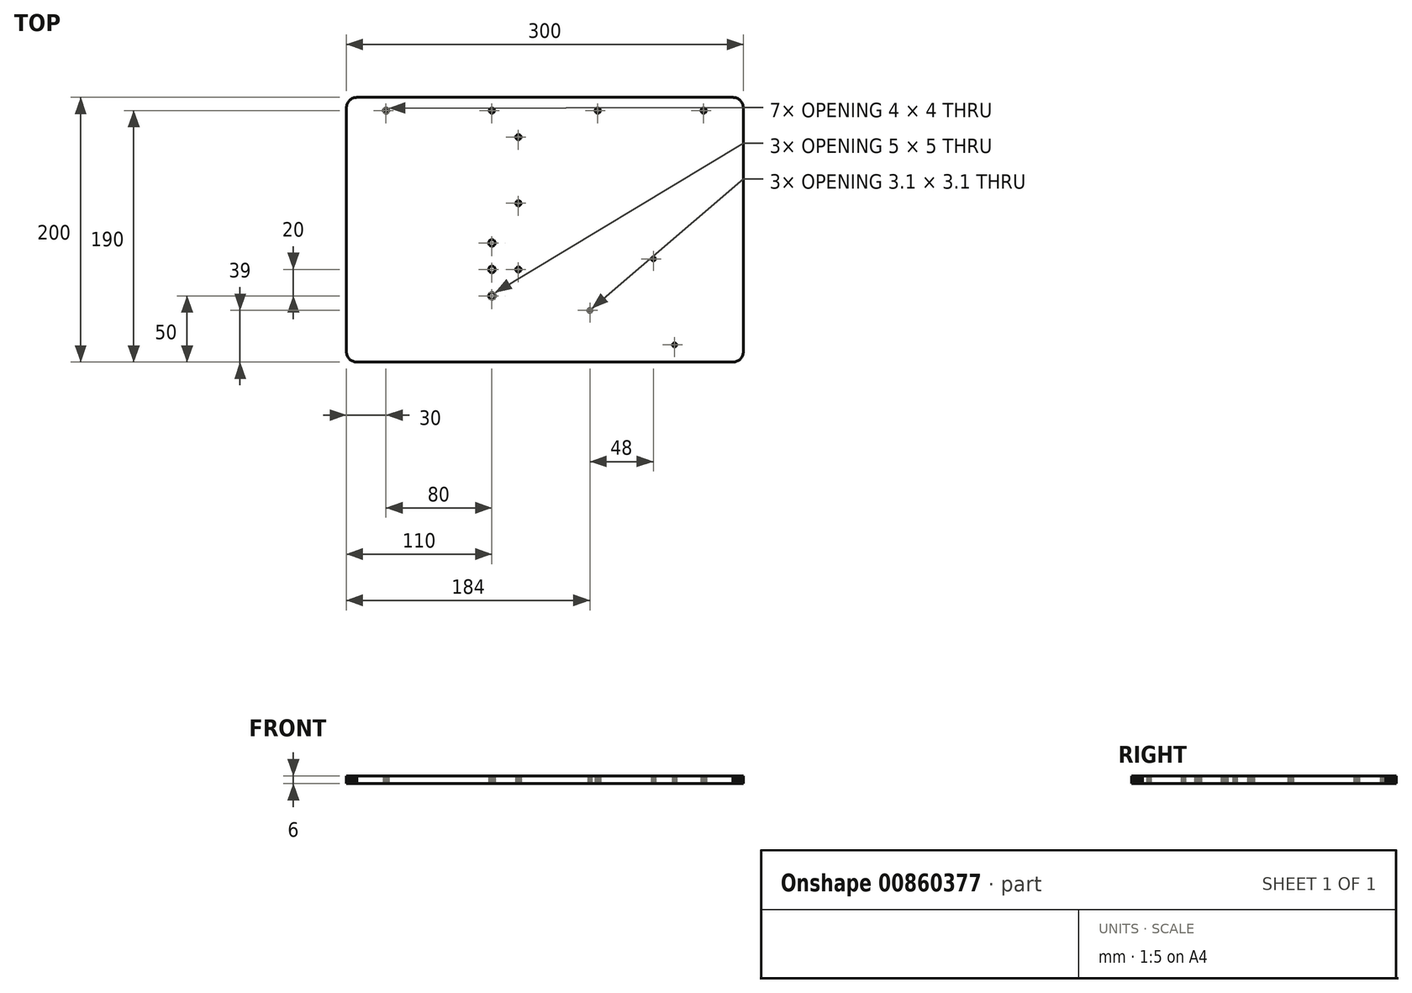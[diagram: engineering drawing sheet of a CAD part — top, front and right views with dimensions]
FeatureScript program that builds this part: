
annotation { "Feature Type Name" : "Feature", "Feature Type Description" : "" }
export const myFeature = defineFeature(function(context is Context, id is Id, definition is map)
    precondition{}
    {
        {
            var Q0;
            Q0=qCreatedBy(makeId("Top.planeOp"),FACE);
            var sketch = newSketch(context, id + "F0", { "sketchPlane" : qUnion([Q0])});
            skLineSegment(sketch, "E0", {"start": v(142.78, -99.96) * mm, "end": v(143.56, -99.85) * mm});
            skLineSegment(sketch, "E1", {"start": v(143.56, -99.85) * mm, "end": v(144.32, -99.66) * mm});
            skLineSegment(sketch, "E2", {"start": v(144.32, -99.66) * mm, "end": v(145.06, -99.4) * mm});
            skLineSegment(sketch, "E3", {"start": v(145.06, -99.4) * mm, "end": v(145.77, -99.06) * mm});
            skLineSegment(sketch, "E4", {"start": v(145.77, -99.06) * mm, "end": v(146.44, -98.65) * mm});
            skLineSegment(sketch, "E5", {"start": v(146.44, -98.65) * mm, "end": v(147.07, -98.18) * mm});
            skLineSegment(sketch, "E6", {"start": v(147.07, -98.18) * mm, "end": v(147.66, -97.66) * mm});
            skLineSegment(sketch, "E7", {"start": v(147.66, -97.66) * mm, "end": v(148.18, -97.08) * mm});
            skLineSegment(sketch, "E8", {"start": v(148.18, -97.08) * mm, "end": v(148.65, -96.44) * mm});
            skLineSegment(sketch, "E9", {"start": v(148.65, -96.44) * mm, "end": v(149.06, -95.77) * mm});
            skLineSegment(sketch, "E10", {"start": v(149.06, -95.77) * mm, "end": v(149.4, -95.06) * mm});
            skLineSegment(sketch, "E11", {"start": v(149.4, -95.06) * mm, "end": v(149.66, -94.32) * mm});
            skLineSegment(sketch, "E12", {"start": v(149.66, -94.32) * mm, "end": v(149.85, -93.56) * mm});
            skLineSegment(sketch, "E13", {"start": v(149.85, -93.56) * mm, "end": v(149.96, -92.78) * mm});
            skLineSegment(sketch, "E14", {"start": v(149.96, -92.78) * mm, "end": v(150, -92) * mm});
            skLineSegment(sketch, "E15", {"start": v(150, -92) * mm, "end": v(150, 92) * mm});
            skLineSegment(sketch, "E16", {"start": v(150, 92) * mm, "end": v(149.96, 92.78) * mm});
            skLineSegment(sketch, "E17", {"start": v(149.96, 92.78) * mm, "end": v(149.85, 93.56) * mm});
            skLineSegment(sketch, "E18", {"start": v(149.85, 93.56) * mm, "end": v(149.66, 94.32) * mm});
            skLineSegment(sketch, "E19", {"start": v(149.66, 94.32) * mm, "end": v(149.4, 95.06) * mm});
            skLineSegment(sketch, "E20", {"start": v(149.4, 95.06) * mm, "end": v(149.06, 95.77) * mm});
            skLineSegment(sketch, "E21", {"start": v(149.06, 95.77) * mm, "end": v(148.65, 96.44) * mm});
            skLineSegment(sketch, "E22", {"start": v(148.65, 96.44) * mm, "end": v(148.18, 97.07) * mm});
            skLineSegment(sketch, "E23", {"start": v(148.18, 97.07) * mm, "end": v(147.66, 97.66) * mm});
            skLineSegment(sketch, "E24", {"start": v(147.66, 97.66) * mm, "end": v(147.07, 98.18) * mm});
            skLineSegment(sketch, "E25", {"start": v(147.07, 98.18) * mm, "end": v(146.44, 98.65) * mm});
            skLineSegment(sketch, "E26", {"start": v(146.44, 98.65) * mm, "end": v(145.77, 99.06) * mm});
            skLineSegment(sketch, "E27", {"start": v(145.77, 99.06) * mm, "end": v(145.06, 99.4) * mm});
            skLineSegment(sketch, "E28", {"start": v(145.06, 99.4) * mm, "end": v(144.32, 99.66) * mm});
            skLineSegment(sketch, "E29", {"start": v(144.32, 99.66) * mm, "end": v(143.56, 99.85) * mm});
            skLineSegment(sketch, "E30", {"start": v(143.56, 99.85) * mm, "end": v(142.78, 99.96) * mm});
            skLineSegment(sketch, "E31", {"start": v(142.78, 99.96) * mm, "end": v(142, 100) * mm});
            skLineSegment(sketch, "E32", {"start": v(142, 100) * mm, "end": v(-142, 100) * mm});
            skLineSegment(sketch, "E33", {"start": v(-142, 100) * mm, "end": v(-142.78, 99.96) * mm});
            skLineSegment(sketch, "E34", {"start": v(-142.78, 99.96) * mm, "end": v(-143.56, 99.85) * mm});
            skLineSegment(sketch, "E35", {"start": v(-143.56, 99.85) * mm, "end": v(-144.32, 99.66) * mm});
            skLineSegment(sketch, "E36", {"start": v(-144.32, 99.66) * mm, "end": v(-145.06, 99.4) * mm});
            skLineSegment(sketch, "E37", {"start": v(-145.06, 99.4) * mm, "end": v(-145.77, 99.06) * mm});
            skLineSegment(sketch, "E38", {"start": v(-145.77, 99.06) * mm, "end": v(-146.44, 98.65) * mm});
            skLineSegment(sketch, "E39", {"start": v(-146.44, 98.65) * mm, "end": v(-147.08, 98.18) * mm});
            skLineSegment(sketch, "E40", {"start": v(-147.08, 98.18) * mm, "end": v(-147.66, 97.66) * mm});
            skLineSegment(sketch, "E41", {"start": v(-147.66, 97.66) * mm, "end": v(-148.18, 97.07) * mm});
            skLineSegment(sketch, "E42", {"start": v(-148.18, 97.07) * mm, "end": v(-148.65, 96.44) * mm});
            skLineSegment(sketch, "E43", {"start": v(-148.65, 96.44) * mm, "end": v(-149.06, 95.77) * mm});
            skLineSegment(sketch, "E44", {"start": v(-149.06, 95.77) * mm, "end": v(-149.4, 95.06) * mm});
            skLineSegment(sketch, "E45", {"start": v(-149.4, 95.06) * mm, "end": v(-149.66, 94.32) * mm});
            skLineSegment(sketch, "E46", {"start": v(-149.66, 94.32) * mm, "end": v(-149.85, 93.56) * mm});
            skLineSegment(sketch, "E47", {"start": v(-149.85, 93.56) * mm, "end": v(-149.96, 92.78) * mm});
            skLineSegment(sketch, "E48", {"start": v(-149.96, 92.78) * mm, "end": v(-150, 92) * mm});
            skLineSegment(sketch, "E49", {"start": v(-150, 92) * mm, "end": v(-150, -92) * mm});
            skLineSegment(sketch, "E50", {"start": v(-150, -92) * mm, "end": v(-149.96, -92.78) * mm});
            skLineSegment(sketch, "E51", {"start": v(-149.96, -92.78) * mm, "end": v(-149.85, -93.56) * mm});
            skLineSegment(sketch, "E52", {"start": v(-149.85, -93.56) * mm, "end": v(-149.66, -94.32) * mm});
            skLineSegment(sketch, "E53", {"start": v(-149.66, -94.32) * mm, "end": v(-149.4, -95.06) * mm});
            skLineSegment(sketch, "E54", {"start": v(-149.4, -95.06) * mm, "end": v(-149.06, -95.77) * mm});
            skLineSegment(sketch, "E55", {"start": v(-149.06, -95.77) * mm, "end": v(-148.65, -96.44) * mm});
            skLineSegment(sketch, "E56", {"start": v(-148.65, -96.44) * mm, "end": v(-148.18, -97.08) * mm});
            skLineSegment(sketch, "E57", {"start": v(-148.18, -97.08) * mm, "end": v(-147.66, -97.66) * mm});
            skLineSegment(sketch, "E58", {"start": v(-147.66, -97.66) * mm, "end": v(-147.08, -98.18) * mm});
            skLineSegment(sketch, "E59", {"start": v(-147.08, -98.18) * mm, "end": v(-146.44, -98.65) * mm});
            skLineSegment(sketch, "E60", {"start": v(-146.44, -98.65) * mm, "end": v(-145.77, -99.06) * mm});
            skLineSegment(sketch, "E61", {"start": v(-145.77, -99.06) * mm, "end": v(-145.06, -99.4) * mm});
            skLineSegment(sketch, "E62", {"start": v(-145.06, -99.4) * mm, "end": v(-144.32, -99.66) * mm});
            skLineSegment(sketch, "E63", {"start": v(-144.32, -99.66) * mm, "end": v(-143.56, -99.85) * mm});
            skLineSegment(sketch, "E64", {"start": v(-143.56, -99.85) * mm, "end": v(-142.78, -99.96) * mm});
            skLineSegment(sketch, "E65", {"start": v(-142.78, -99.96) * mm, "end": v(-142, -100) * mm});
            skLineSegment(sketch, "E66", {"start": v(-142, -100) * mm, "end": v(142, -100) * mm});
            skLineSegment(sketch, "E67", {"start": v(142, -100) * mm, "end": v(142.78, -99.96) * mm});
            skLineSegment(sketch, "E68", {"start": v(-120.2, 88) * mm, "end": v(-120.4, 88.04) * mm});
            skLineSegment(sketch, "E69", {"start": v(-120.4, 88.04) * mm, "end": v(-120.58, 88.09) * mm});
            skLineSegment(sketch, "E70", {"start": v(-120.58, 88.09) * mm, "end": v(-120.77, 88.15) * mm});
            skLineSegment(sketch, "E71", {"start": v(-120.77, 88.15) * mm, "end": v(-120.94, 88.24) * mm});
            skLineSegment(sketch, "E72", {"start": v(-120.94, 88.24) * mm, "end": v(-121.11, 88.34) * mm});
            skLineSegment(sketch, "E73", {"start": v(-121.11, 88.34) * mm, "end": v(-121.27, 88.45) * mm});
            skLineSegment(sketch, "E74", {"start": v(-121.27, 88.45) * mm, "end": v(-121.41, 88.59) * mm});
            skLineSegment(sketch, "E75", {"start": v(-121.41, 88.59) * mm, "end": v(-121.55, 88.73) * mm});
            skLineSegment(sketch, "E76", {"start": v(-121.55, 88.73) * mm, "end": v(-121.66, 88.89) * mm});
            skLineSegment(sketch, "E77", {"start": v(-121.66, 88.89) * mm, "end": v(-121.76, 89.06) * mm});
            skLineSegment(sketch, "E78", {"start": v(-121.76, 89.06) * mm, "end": v(-121.85, 89.24) * mm});
            skLineSegment(sketch, "E79", {"start": v(-121.85, 89.24) * mm, "end": v(-121.91, 89.42) * mm});
            skLineSegment(sketch, "E80", {"start": v(-121.91, 89.42) * mm, "end": v(-121.96, 89.61) * mm});
            skLineSegment(sketch, "E81", {"start": v(-121.96, 89.61) * mm, "end": v(-122, 89.8) * mm});
            skLineSegment(sketch, "E82", {"start": v(-122, 89.8) * mm, "end": v(-122, 90) * mm});
            skLineSegment(sketch, "E83", {"start": v(-122, 90) * mm, "end": v(-122, 90.2) * mm});
            skLineSegment(sketch, "E84", {"start": v(-122, 90.2) * mm, "end": v(-121.96, 90.39) * mm});
            skLineSegment(sketch, "E85", {"start": v(-121.96, 90.39) * mm, "end": v(-121.91, 90.58) * mm});
            skLineSegment(sketch, "E86", {"start": v(-121.91, 90.58) * mm, "end": v(-121.85, 90.76) * mm});
            skLineSegment(sketch, "E87", {"start": v(-121.85, 90.76) * mm, "end": v(-121.76, 90.94) * mm});
            skLineSegment(sketch, "E88", {"start": v(-121.76, 90.94) * mm, "end": v(-121.66, 91.11) * mm});
            skLineSegment(sketch, "E89", {"start": v(-121.66, 91.11) * mm, "end": v(-121.55, 91.27) * mm});
            skLineSegment(sketch, "E90", {"start": v(-121.55, 91.27) * mm, "end": v(-121.41, 91.41) * mm});
            skLineSegment(sketch, "E91", {"start": v(-121.41, 91.41) * mm, "end": v(-121.27, 91.55) * mm});
            skLineSegment(sketch, "E92", {"start": v(-121.27, 91.55) * mm, "end": v(-121.11, 91.66) * mm});
            skLineSegment(sketch, "E93", {"start": v(-121.11, 91.66) * mm, "end": v(-120.94, 91.76) * mm});
            skLineSegment(sketch, "E94", {"start": v(-120.94, 91.76) * mm, "end": v(-120.77, 91.85) * mm});
            skLineSegment(sketch, "E95", {"start": v(-120.77, 91.85) * mm, "end": v(-120.58, 91.91) * mm});
            skLineSegment(sketch, "E96", {"start": v(-120.58, 91.91) * mm, "end": v(-120.4, 91.96) * mm});
            skLineSegment(sketch, "E97", {"start": v(-120.4, 91.96) * mm, "end": v(-120.2, 92) * mm});
            skLineSegment(sketch, "E98", {"start": v(-120.2, 92) * mm, "end": v(-120, 92) * mm});
            skLineSegment(sketch, "E99", {"start": v(-120, 92) * mm, "end": v(-119.8, 92) * mm});
            skLineSegment(sketch, "E100", {"start": v(-119.8, 92) * mm, "end": v(-119.6, 91.96) * mm});
            skLineSegment(sketch, "E101", {"start": v(-119.6, 91.96) * mm, "end": v(-119.42, 91.91) * mm});
            skLineSegment(sketch, "E102", {"start": v(-119.42, 91.91) * mm, "end": v(-119.23, 91.85) * mm});
            skLineSegment(sketch, "E103", {"start": v(-119.23, 91.85) * mm, "end": v(-119.06, 91.76) * mm});
            skLineSegment(sketch, "E104", {"start": v(-119.06, 91.76) * mm, "end": v(-118.89, 91.66) * mm});
            skLineSegment(sketch, "E105", {"start": v(-118.89, 91.66) * mm, "end": v(-118.73, 91.55) * mm});
            skLineSegment(sketch, "E106", {"start": v(-118.73, 91.55) * mm, "end": v(-118.59, 91.41) * mm});
            skLineSegment(sketch, "E107", {"start": v(-118.59, 91.41) * mm, "end": v(-118.45, 91.27) * mm});
            skLineSegment(sketch, "E108", {"start": v(-118.45, 91.27) * mm, "end": v(-118.34, 91.11) * mm});
            skLineSegment(sketch, "E109", {"start": v(-118.34, 91.11) * mm, "end": v(-118.24, 90.94) * mm});
            skLineSegment(sketch, "E110", {"start": v(-118.24, 90.94) * mm, "end": v(-118.15, 90.76) * mm});
            skLineSegment(sketch, "E111", {"start": v(-118.15, 90.76) * mm, "end": v(-118.09, 90.58) * mm});
            skLineSegment(sketch, "E112", {"start": v(-118.09, 90.58) * mm, "end": v(-118.04, 90.39) * mm});
            skLineSegment(sketch, "E113", {"start": v(-118.04, 90.39) * mm, "end": v(-118, 90.2) * mm});
            skLineSegment(sketch, "E114", {"start": v(-118, 90.2) * mm, "end": v(-118, 90) * mm});
            skLineSegment(sketch, "E115", {"start": v(-118, 90) * mm, "end": v(-118, 89.8) * mm});
            skLineSegment(sketch, "E116", {"start": v(-118, 89.8) * mm, "end": v(-118.04, 89.61) * mm});
            skLineSegment(sketch, "E117", {"start": v(-118.04, 89.61) * mm, "end": v(-118.09, 89.42) * mm});
            skLineSegment(sketch, "E118", {"start": v(-118.09, 89.42) * mm, "end": v(-118.15, 89.24) * mm});
            skLineSegment(sketch, "E119", {"start": v(-118.15, 89.24) * mm, "end": v(-118.24, 89.06) * mm});
            skLineSegment(sketch, "E120", {"start": v(-118.24, 89.06) * mm, "end": v(-118.34, 88.89) * mm});
            skLineSegment(sketch, "E121", {"start": v(-118.34, 88.89) * mm, "end": v(-118.45, 88.73) * mm});
            skLineSegment(sketch, "E122", {"start": v(-118.45, 88.73) * mm, "end": v(-118.59, 88.59) * mm});
            skLineSegment(sketch, "E123", {"start": v(-118.59, 88.59) * mm, "end": v(-118.73, 88.45) * mm});
            skLineSegment(sketch, "E124", {"start": v(-118.73, 88.45) * mm, "end": v(-118.89, 88.34) * mm});
            skLineSegment(sketch, "E125", {"start": v(-118.89, 88.34) * mm, "end": v(-119.06, 88.24) * mm});
            skLineSegment(sketch, "E126", {"start": v(-119.06, 88.24) * mm, "end": v(-119.23, 88.15) * mm});
            skLineSegment(sketch, "E127", {"start": v(-119.23, 88.15) * mm, "end": v(-119.42, 88.09) * mm});
            skLineSegment(sketch, "E128", {"start": v(-119.42, 88.09) * mm, "end": v(-119.6, 88.04) * mm});
            skLineSegment(sketch, "E129", {"start": v(-119.6, 88.04) * mm, "end": v(-119.8, 88) * mm});
            skLineSegment(sketch, "E130", {"start": v(-119.8, 88) * mm, "end": v(-120, 88) * mm});
            skLineSegment(sketch, "E131", {"start": v(-120, 88) * mm, "end": v(-120.2, 88) * mm});
            skLineSegment(sketch, "E132", {"start": v(-40.2, 88) * mm, "end": v(-40.4, 88.04) * mm});
            skLineSegment(sketch, "E133", {"start": v(-40.4, 88.04) * mm, "end": v(-40.58, 88.09) * mm});
            skLineSegment(sketch, "E134", {"start": v(-40.58, 88.09) * mm, "end": v(-40.77, 88.15) * mm});
            skLineSegment(sketch, "E135", {"start": v(-40.77, 88.15) * mm, "end": v(-40.94, 88.24) * mm});
            skLineSegment(sketch, "E136", {"start": v(-40.94, 88.24) * mm, "end": v(-41.11, 88.34) * mm});
            skLineSegment(sketch, "E137", {"start": v(-41.11, 88.34) * mm, "end": v(-41.27, 88.45) * mm});
            skLineSegment(sketch, "E138", {"start": v(-41.27, 88.45) * mm, "end": v(-41.41, 88.59) * mm});
            skLineSegment(sketch, "E139", {"start": v(-41.41, 88.59) * mm, "end": v(-41.55, 88.73) * mm});
            skLineSegment(sketch, "E140", {"start": v(-41.55, 88.73) * mm, "end": v(-41.66, 88.89) * mm});
            skLineSegment(sketch, "E141", {"start": v(-41.66, 88.89) * mm, "end": v(-41.76, 89.06) * mm});
            skLineSegment(sketch, "E142", {"start": v(-41.76, 89.06) * mm, "end": v(-41.85, 89.24) * mm});
            skLineSegment(sketch, "E143", {"start": v(-41.85, 89.24) * mm, "end": v(-41.91, 89.42) * mm});
            skLineSegment(sketch, "E144", {"start": v(-41.91, 89.42) * mm, "end": v(-41.96, 89.61) * mm});
            skLineSegment(sketch, "E145", {"start": v(-41.96, 89.61) * mm, "end": v(-41.99, 89.8) * mm});
            skLineSegment(sketch, "E146", {"start": v(-41.99, 89.8) * mm, "end": v(-42, 90) * mm});
            skLineSegment(sketch, "E147", {"start": v(-42, 90) * mm, "end": v(-41.99, 90.2) * mm});
            skLineSegment(sketch, "E148", {"start": v(-41.99, 90.2) * mm, "end": v(-41.96, 90.39) * mm});
            skLineSegment(sketch, "E149", {"start": v(-41.96, 90.39) * mm, "end": v(-41.91, 90.58) * mm});
            skLineSegment(sketch, "E150", {"start": v(-41.91, 90.58) * mm, "end": v(-41.85, 90.76) * mm});
            skLineSegment(sketch, "E151", {"start": v(-41.85, 90.76) * mm, "end": v(-41.76, 90.94) * mm});
            skLineSegment(sketch, "E152", {"start": v(-41.76, 90.94) * mm, "end": v(-41.66, 91.11) * mm});
            skLineSegment(sketch, "E153", {"start": v(-41.66, 91.11) * mm, "end": v(-41.55, 91.27) * mm});
            skLineSegment(sketch, "E154", {"start": v(-41.55, 91.27) * mm, "end": v(-41.41, 91.41) * mm});
            skLineSegment(sketch, "E155", {"start": v(-41.41, 91.41) * mm, "end": v(-41.27, 91.55) * mm});
            skLineSegment(sketch, "E156", {"start": v(-41.27, 91.55) * mm, "end": v(-41.11, 91.66) * mm});
            skLineSegment(sketch, "E157", {"start": v(-41.11, 91.66) * mm, "end": v(-40.94, 91.76) * mm});
            skLineSegment(sketch, "E158", {"start": v(-40.94, 91.76) * mm, "end": v(-40.77, 91.85) * mm});
            skLineSegment(sketch, "E159", {"start": v(-40.77, 91.85) * mm, "end": v(-40.58, 91.91) * mm});
            skLineSegment(sketch, "E160", {"start": v(-40.58, 91.91) * mm, "end": v(-40.4, 91.96) * mm});
            skLineSegment(sketch, "E161", {"start": v(-40.4, 91.96) * mm, "end": v(-40.2, 92) * mm});
            skLineSegment(sketch, "E162", {"start": v(-40.2, 92) * mm, "end": v(-40, 92) * mm});
            skLineSegment(sketch, "E163", {"start": v(-40, 92) * mm, "end": v(-39.8, 92) * mm});
            skLineSegment(sketch, "E164", {"start": v(-39.8, 92) * mm, "end": v(-39.6, 91.96) * mm});
            skLineSegment(sketch, "E165", {"start": v(-39.6, 91.96) * mm, "end": v(-39.42, 91.91) * mm});
            skLineSegment(sketch, "E166", {"start": v(-39.42, 91.91) * mm, "end": v(-39.23, 91.85) * mm});
            skLineSegment(sketch, "E167", {"start": v(-39.23, 91.85) * mm, "end": v(-39.06, 91.76) * mm});
            skLineSegment(sketch, "E168", {"start": v(-39.06, 91.76) * mm, "end": v(-38.89, 91.66) * mm});
            skLineSegment(sketch, "E169", {"start": v(-38.89, 91.66) * mm, "end": v(-38.73, 91.55) * mm});
            skLineSegment(sketch, "E170", {"start": v(-38.73, 91.55) * mm, "end": v(-38.59, 91.41) * mm});
            skLineSegment(sketch, "E171", {"start": v(-38.59, 91.41) * mm, "end": v(-38.45, 91.27) * mm});
            skLineSegment(sketch, "E172", {"start": v(-38.45, 91.27) * mm, "end": v(-38.34, 91.11) * mm});
            skLineSegment(sketch, "E173", {"start": v(-38.34, 91.11) * mm, "end": v(-38.24, 90.94) * mm});
            skLineSegment(sketch, "E174", {"start": v(-38.24, 90.94) * mm, "end": v(-38.15, 90.76) * mm});
            skLineSegment(sketch, "E175", {"start": v(-38.15, 90.76) * mm, "end": v(-38.09, 90.58) * mm});
            skLineSegment(sketch, "E176", {"start": v(-38.09, 90.58) * mm, "end": v(-38.04, 90.39) * mm});
            skLineSegment(sketch, "E177", {"start": v(-38.04, 90.39) * mm, "end": v(-38.01, 90.2) * mm});
            skLineSegment(sketch, "E178", {"start": v(-38.01, 90.2) * mm, "end": v(-38, 90) * mm});
            skLineSegment(sketch, "E179", {"start": v(-38, 90) * mm, "end": v(-38.01, 89.8) * mm});
            skLineSegment(sketch, "E180", {"start": v(-38.01, 89.8) * mm, "end": v(-38.04, 89.61) * mm});
            skLineSegment(sketch, "E181", {"start": v(-38.04, 89.61) * mm, "end": v(-38.09, 89.42) * mm});
            skLineSegment(sketch, "E182", {"start": v(-38.09, 89.42) * mm, "end": v(-38.15, 89.24) * mm});
            skLineSegment(sketch, "E183", {"start": v(-38.15, 89.24) * mm, "end": v(-38.24, 89.06) * mm});
            skLineSegment(sketch, "E184", {"start": v(-38.24, 89.06) * mm, "end": v(-38.34, 88.89) * mm});
            skLineSegment(sketch, "E185", {"start": v(-38.34, 88.89) * mm, "end": v(-38.45, 88.73) * mm});
            skLineSegment(sketch, "E186", {"start": v(-38.45, 88.73) * mm, "end": v(-38.59, 88.59) * mm});
            skLineSegment(sketch, "E187", {"start": v(-38.59, 88.59) * mm, "end": v(-38.73, 88.45) * mm});
            skLineSegment(sketch, "E188", {"start": v(-38.73, 88.45) * mm, "end": v(-38.89, 88.34) * mm});
            skLineSegment(sketch, "E189", {"start": v(-38.89, 88.34) * mm, "end": v(-39.06, 88.24) * mm});
            skLineSegment(sketch, "E190", {"start": v(-39.06, 88.24) * mm, "end": v(-39.23, 88.15) * mm});
            skLineSegment(sketch, "E191", {"start": v(-39.23, 88.15) * mm, "end": v(-39.42, 88.09) * mm});
            skLineSegment(sketch, "E192", {"start": v(-39.42, 88.09) * mm, "end": v(-39.6, 88.04) * mm});
            skLineSegment(sketch, "E193", {"start": v(-39.6, 88.04) * mm, "end": v(-39.8, 88) * mm});
            skLineSegment(sketch, "E194", {"start": v(-39.8, 88) * mm, "end": v(-40, 88) * mm});
            skLineSegment(sketch, "E195", {"start": v(-40, 88) * mm, "end": v(-40.2, 88) * mm});
            skLineSegment(sketch, "E196", {"start": v(39.8, 88) * mm, "end": v(39.61, 88.04) * mm});
            skLineSegment(sketch, "E197", {"start": v(39.61, 88.04) * mm, "end": v(39.42, 88.09) * mm});
            skLineSegment(sketch, "E198", {"start": v(39.42, 88.09) * mm, "end": v(39.24, 88.15) * mm});
            skLineSegment(sketch, "E199", {"start": v(39.24, 88.15) * mm, "end": v(39.06, 88.24) * mm});
            skLineSegment(sketch, "E200", {"start": v(39.06, 88.24) * mm, "end": v(38.89, 88.34) * mm});
            skLineSegment(sketch, "E201", {"start": v(38.89, 88.34) * mm, "end": v(38.73, 88.45) * mm});
            skLineSegment(sketch, "E202", {"start": v(38.73, 88.45) * mm, "end": v(38.59, 88.59) * mm});
            skLineSegment(sketch, "E203", {"start": v(38.59, 88.59) * mm, "end": v(38.45, 88.73) * mm});
            skLineSegment(sketch, "E204", {"start": v(38.45, 88.73) * mm, "end": v(38.34, 88.89) * mm});
            skLineSegment(sketch, "E205", {"start": v(38.34, 88.89) * mm, "end": v(38.24, 89.06) * mm});
            skLineSegment(sketch, "E206", {"start": v(38.24, 89.06) * mm, "end": v(38.15, 89.24) * mm});
            skLineSegment(sketch, "E207", {"start": v(38.15, 89.24) * mm, "end": v(38.09, 89.42) * mm});
            skLineSegment(sketch, "E208", {"start": v(38.09, 89.42) * mm, "end": v(38.04, 89.61) * mm});
            skLineSegment(sketch, "E209", {"start": v(38.04, 89.61) * mm, "end": v(38, 89.8) * mm});
            skLineSegment(sketch, "E210", {"start": v(38, 89.8) * mm, "end": v(38, 90) * mm});
            skLineSegment(sketch, "E211", {"start": v(38, 90) * mm, "end": v(38, 90.2) * mm});
            skLineSegment(sketch, "E212", {"start": v(38, 90.2) * mm, "end": v(38.04, 90.39) * mm});
            skLineSegment(sketch, "E213", {"start": v(38.04, 90.39) * mm, "end": v(38.09, 90.58) * mm});
            skLineSegment(sketch, "E214", {"start": v(38.09, 90.58) * mm, "end": v(38.15, 90.76) * mm});
            skLineSegment(sketch, "E215", {"start": v(38.15, 90.76) * mm, "end": v(38.24, 90.94) * mm});
            skLineSegment(sketch, "E216", {"start": v(38.24, 90.94) * mm, "end": v(38.34, 91.11) * mm});
            skLineSegment(sketch, "E217", {"start": v(38.34, 91.11) * mm, "end": v(38.45, 91.27) * mm});
            skLineSegment(sketch, "E218", {"start": v(38.45, 91.27) * mm, "end": v(38.59, 91.41) * mm});
            skLineSegment(sketch, "E219", {"start": v(38.59, 91.41) * mm, "end": v(38.73, 91.55) * mm});
            skLineSegment(sketch, "E220", {"start": v(38.73, 91.55) * mm, "end": v(38.89, 91.66) * mm});
            skLineSegment(sketch, "E221", {"start": v(38.89, 91.66) * mm, "end": v(39.06, 91.76) * mm});
            skLineSegment(sketch, "E222", {"start": v(39.06, 91.76) * mm, "end": v(39.24, 91.85) * mm});
            skLineSegment(sketch, "E223", {"start": v(39.24, 91.85) * mm, "end": v(39.42, 91.91) * mm});
            skLineSegment(sketch, "E224", {"start": v(39.42, 91.91) * mm, "end": v(39.61, 91.96) * mm});
            skLineSegment(sketch, "E225", {"start": v(39.61, 91.96) * mm, "end": v(39.8, 92) * mm});
            skLineSegment(sketch, "E226", {"start": v(39.8, 92) * mm, "end": v(40, 92) * mm});
            skLineSegment(sketch, "E227", {"start": v(40, 92) * mm, "end": v(40.2, 92) * mm});
            skLineSegment(sketch, "E228", {"start": v(40.2, 92) * mm, "end": v(40.39, 91.96) * mm});
            skLineSegment(sketch, "E229", {"start": v(40.39, 91.96) * mm, "end": v(40.58, 91.91) * mm});
            skLineSegment(sketch, "E230", {"start": v(40.58, 91.91) * mm, "end": v(40.76, 91.85) * mm});
            skLineSegment(sketch, "E231", {"start": v(40.76, 91.85) * mm, "end": v(40.94, 91.76) * mm});
            skLineSegment(sketch, "E232", {"start": v(40.94, 91.76) * mm, "end": v(41.11, 91.66) * mm});
            skLineSegment(sketch, "E233", {"start": v(41.11, 91.66) * mm, "end": v(41.27, 91.55) * mm});
            skLineSegment(sketch, "E234", {"start": v(41.27, 91.55) * mm, "end": v(41.41, 91.41) * mm});
            skLineSegment(sketch, "E235", {"start": v(41.41, 91.41) * mm, "end": v(41.55, 91.27) * mm});
            skLineSegment(sketch, "E236", {"start": v(41.55, 91.27) * mm, "end": v(41.66, 91.11) * mm});
            skLineSegment(sketch, "E237", {"start": v(41.66, 91.11) * mm, "end": v(41.76, 90.94) * mm});
            skLineSegment(sketch, "E238", {"start": v(41.76, 90.94) * mm, "end": v(41.85, 90.76) * mm});
            skLineSegment(sketch, "E239", {"start": v(41.85, 90.76) * mm, "end": v(41.91, 90.58) * mm});
            skLineSegment(sketch, "E240", {"start": v(41.91, 90.58) * mm, "end": v(41.96, 90.39) * mm});
            skLineSegment(sketch, "E241", {"start": v(41.96, 90.39) * mm, "end": v(42, 90.2) * mm});
            skLineSegment(sketch, "E242", {"start": v(42, 90.2) * mm, "end": v(42, 90) * mm});
            skLineSegment(sketch, "E243", {"start": v(42, 90) * mm, "end": v(42, 89.8) * mm});
            skLineSegment(sketch, "E244", {"start": v(42, 89.8) * mm, "end": v(41.96, 89.61) * mm});
            skLineSegment(sketch, "E245", {"start": v(41.96, 89.61) * mm, "end": v(41.91, 89.42) * mm});
            skLineSegment(sketch, "E246", {"start": v(41.91, 89.42) * mm, "end": v(41.85, 89.24) * mm});
            skLineSegment(sketch, "E247", {"start": v(41.85, 89.24) * mm, "end": v(41.76, 89.06) * mm});
            skLineSegment(sketch, "E248", {"start": v(41.76, 89.06) * mm, "end": v(41.66, 88.89) * mm});
            skLineSegment(sketch, "E249", {"start": v(41.66, 88.89) * mm, "end": v(41.55, 88.73) * mm});
            skLineSegment(sketch, "E250", {"start": v(41.55, 88.73) * mm, "end": v(41.41, 88.59) * mm});
            skLineSegment(sketch, "E251", {"start": v(41.41, 88.59) * mm, "end": v(41.27, 88.45) * mm});
            skLineSegment(sketch, "E252", {"start": v(41.27, 88.45) * mm, "end": v(41.11, 88.34) * mm});
            skLineSegment(sketch, "E253", {"start": v(41.11, 88.34) * mm, "end": v(40.94, 88.24) * mm});
            skLineSegment(sketch, "E254", {"start": v(40.94, 88.24) * mm, "end": v(40.76, 88.15) * mm});
            skLineSegment(sketch, "E255", {"start": v(40.76, 88.15) * mm, "end": v(40.58, 88.09) * mm});
            skLineSegment(sketch, "E256", {"start": v(40.58, 88.09) * mm, "end": v(40.39, 88.04) * mm});
            skLineSegment(sketch, "E257", {"start": v(40.39, 88.04) * mm, "end": v(40.2, 88) * mm});
            skLineSegment(sketch, "E258", {"start": v(40.2, 88) * mm, "end": v(40, 88) * mm});
            skLineSegment(sketch, "E259", {"start": v(40, 88) * mm, "end": v(39.8, 88) * mm});
            skLineSegment(sketch, "E260", {"start": v(119.8, 88) * mm, "end": v(119.61, 88.04) * mm});
            skLineSegment(sketch, "E261", {"start": v(119.61, 88.04) * mm, "end": v(119.42, 88.09) * mm});
            skLineSegment(sketch, "E262", {"start": v(119.42, 88.09) * mm, "end": v(119.24, 88.15) * mm});
            skLineSegment(sketch, "E263", {"start": v(119.24, 88.15) * mm, "end": v(119.06, 88.24) * mm});
            skLineSegment(sketch, "E264", {"start": v(119.06, 88.24) * mm, "end": v(118.89, 88.34) * mm});
            skLineSegment(sketch, "E265", {"start": v(118.89, 88.34) * mm, "end": v(118.73, 88.45) * mm});
            skLineSegment(sketch, "E266", {"start": v(118.73, 88.45) * mm, "end": v(118.59, 88.59) * mm});
            skLineSegment(sketch, "E267", {"start": v(118.59, 88.59) * mm, "end": v(118.45, 88.73) * mm});
            skLineSegment(sketch, "E268", {"start": v(118.45, 88.73) * mm, "end": v(118.34, 88.89) * mm});
            skLineSegment(sketch, "E269", {"start": v(118.34, 88.89) * mm, "end": v(118.24, 89.06) * mm});
            skLineSegment(sketch, "E270", {"start": v(118.24, 89.06) * mm, "end": v(118.15, 89.24) * mm});
            skLineSegment(sketch, "E271", {"start": v(118.15, 89.24) * mm, "end": v(118.09, 89.42) * mm});
            skLineSegment(sketch, "E272", {"start": v(118.09, 89.42) * mm, "end": v(118.04, 89.61) * mm});
            skLineSegment(sketch, "E273", {"start": v(118.04, 89.61) * mm, "end": v(118, 89.8) * mm});
            skLineSegment(sketch, "E274", {"start": v(118, 89.8) * mm, "end": v(118, 90) * mm});
            skLineSegment(sketch, "E275", {"start": v(118, 90) * mm, "end": v(118, 90.2) * mm});
            skLineSegment(sketch, "E276", {"start": v(118, 90.2) * mm, "end": v(118.04, 90.39) * mm});
            skLineSegment(sketch, "E277", {"start": v(118.04, 90.39) * mm, "end": v(118.09, 90.58) * mm});
            skLineSegment(sketch, "E278", {"start": v(118.09, 90.58) * mm, "end": v(118.15, 90.76) * mm});
            skLineSegment(sketch, "E279", {"start": v(118.15, 90.76) * mm, "end": v(118.24, 90.94) * mm});
            skLineSegment(sketch, "E280", {"start": v(118.24, 90.94) * mm, "end": v(118.34, 91.11) * mm});
            skLineSegment(sketch, "E281", {"start": v(118.34, 91.11) * mm, "end": v(118.45, 91.27) * mm});
            skLineSegment(sketch, "E282", {"start": v(118.45, 91.27) * mm, "end": v(118.59, 91.41) * mm});
            skLineSegment(sketch, "E283", {"start": v(118.59, 91.41) * mm, "end": v(118.73, 91.55) * mm});
            skLineSegment(sketch, "E284", {"start": v(118.73, 91.55) * mm, "end": v(118.89, 91.66) * mm});
            skLineSegment(sketch, "E285", {"start": v(118.89, 91.66) * mm, "end": v(119.06, 91.76) * mm});
            skLineSegment(sketch, "E286", {"start": v(119.06, 91.76) * mm, "end": v(119.24, 91.85) * mm});
            skLineSegment(sketch, "E287", {"start": v(119.24, 91.85) * mm, "end": v(119.42, 91.91) * mm});
            skLineSegment(sketch, "E288", {"start": v(119.42, 91.91) * mm, "end": v(119.61, 91.96) * mm});
            skLineSegment(sketch, "E289", {"start": v(119.61, 91.96) * mm, "end": v(119.8, 92) * mm});
            skLineSegment(sketch, "E290", {"start": v(119.8, 92) * mm, "end": v(120, 92) * mm});
            skLineSegment(sketch, "E291", {"start": v(120, 92) * mm, "end": v(120.2, 92) * mm});
            skLineSegment(sketch, "E292", {"start": v(120.2, 92) * mm, "end": v(120.39, 91.96) * mm});
            skLineSegment(sketch, "E293", {"start": v(120.39, 91.96) * mm, "end": v(120.58, 91.91) * mm});
            skLineSegment(sketch, "E294", {"start": v(120.58, 91.91) * mm, "end": v(120.76, 91.85) * mm});
            skLineSegment(sketch, "E295", {"start": v(120.76, 91.85) * mm, "end": v(120.94, 91.76) * mm});
            skLineSegment(sketch, "E296", {"start": v(120.94, 91.76) * mm, "end": v(121.11, 91.66) * mm});
            skLineSegment(sketch, "E297", {"start": v(121.11, 91.66) * mm, "end": v(121.27, 91.55) * mm});
            skLineSegment(sketch, "E298", {"start": v(121.27, 91.55) * mm, "end": v(121.41, 91.41) * mm});
            skLineSegment(sketch, "E299", {"start": v(121.41, 91.41) * mm, "end": v(121.55, 91.27) * mm});
            skLineSegment(sketch, "E300", {"start": v(121.55, 91.27) * mm, "end": v(121.66, 91.11) * mm});
            skLineSegment(sketch, "E301", {"start": v(121.66, 91.11) * mm, "end": v(121.76, 90.94) * mm});
            skLineSegment(sketch, "E302", {"start": v(121.76, 90.94) * mm, "end": v(121.85, 90.76) * mm});
            skLineSegment(sketch, "E303", {"start": v(121.85, 90.76) * mm, "end": v(121.91, 90.58) * mm});
            skLineSegment(sketch, "E304", {"start": v(121.91, 90.58) * mm, "end": v(121.96, 90.39) * mm});
            skLineSegment(sketch, "E305", {"start": v(121.96, 90.39) * mm, "end": v(122, 90.2) * mm});
            skLineSegment(sketch, "E306", {"start": v(122, 90.2) * mm, "end": v(122, 90) * mm});
            skLineSegment(sketch, "E307", {"start": v(122, 90) * mm, "end": v(122, 89.8) * mm});
            skLineSegment(sketch, "E308", {"start": v(122, 89.8) * mm, "end": v(121.96, 89.61) * mm});
            skLineSegment(sketch, "E309", {"start": v(121.96, 89.61) * mm, "end": v(121.91, 89.42) * mm});
            skLineSegment(sketch, "E310", {"start": v(121.91, 89.42) * mm, "end": v(121.85, 89.24) * mm});
            skLineSegment(sketch, "E311", {"start": v(121.85, 89.24) * mm, "end": v(121.76, 89.06) * mm});
            skLineSegment(sketch, "E312", {"start": v(121.76, 89.06) * mm, "end": v(121.66, 88.89) * mm});
            skLineSegment(sketch, "E313", {"start": v(121.66, 88.89) * mm, "end": v(121.55, 88.73) * mm});
            skLineSegment(sketch, "E314", {"start": v(121.55, 88.73) * mm, "end": v(121.41, 88.59) * mm});
            skLineSegment(sketch, "E315", {"start": v(121.41, 88.59) * mm, "end": v(121.27, 88.45) * mm});
            skLineSegment(sketch, "E316", {"start": v(121.27, 88.45) * mm, "end": v(121.11, 88.34) * mm});
            skLineSegment(sketch, "E317", {"start": v(121.11, 88.34) * mm, "end": v(120.94, 88.24) * mm});
            skLineSegment(sketch, "E318", {"start": v(120.94, 88.24) * mm, "end": v(120.76, 88.15) * mm});
            skLineSegment(sketch, "E319", {"start": v(120.76, 88.15) * mm, "end": v(120.58, 88.09) * mm});
            skLineSegment(sketch, "E320", {"start": v(120.58, 88.09) * mm, "end": v(120.39, 88.04) * mm});
            skLineSegment(sketch, "E321", {"start": v(120.39, 88.04) * mm, "end": v(120.2, 88) * mm});
            skLineSegment(sketch, "E322", {"start": v(120.2, 88) * mm, "end": v(120, 88) * mm});
            skLineSegment(sketch, "E323", {"start": v(120, 88) * mm, "end": v(119.8, 88) * mm});
            skLineSegment(sketch, "E324", {"start": v(-20.2, 68) * mm, "end": v(-20.39, 68.04) * mm});
            skLineSegment(sketch, "E325", {"start": v(-20.39, 68.04) * mm, "end": v(-20.58, 68.09) * mm});
            skLineSegment(sketch, "E326", {"start": v(-20.58, 68.09) * mm, "end": v(-20.76, 68.15) * mm});
            skLineSegment(sketch, "E327", {"start": v(-20.76, 68.15) * mm, "end": v(-20.94, 68.24) * mm});
            skLineSegment(sketch, "E328", {"start": v(-20.94, 68.24) * mm, "end": v(-21.11, 68.34) * mm});
            skLineSegment(sketch, "E329", {"start": v(-21.11, 68.34) * mm, "end": v(-21.27, 68.45) * mm});
            skLineSegment(sketch, "E330", {"start": v(-21.27, 68.45) * mm, "end": v(-21.41, 68.59) * mm});
            skLineSegment(sketch, "E331", {"start": v(-21.41, 68.59) * mm, "end": v(-21.55, 68.73) * mm});
            skLineSegment(sketch, "E332", {"start": v(-21.55, 68.73) * mm, "end": v(-21.66, 68.89) * mm});
            skLineSegment(sketch, "E333", {"start": v(-21.66, 68.89) * mm, "end": v(-21.76, 69.06) * mm});
            skLineSegment(sketch, "E334", {"start": v(-21.76, 69.06) * mm, "end": v(-21.85, 69.24) * mm});
            skLineSegment(sketch, "E335", {"start": v(-21.85, 69.24) * mm, "end": v(-21.91, 69.42) * mm});
            skLineSegment(sketch, "E336", {"start": v(-21.91, 69.42) * mm, "end": v(-21.96, 69.61) * mm});
            skLineSegment(sketch, "E337", {"start": v(-21.96, 69.61) * mm, "end": v(-22, 69.8) * mm});
            skLineSegment(sketch, "E338", {"start": v(-22, 69.8) * mm, "end": v(-22, 70) * mm});
            skLineSegment(sketch, "E339", {"start": v(-22, 70) * mm, "end": v(-22, 70.2) * mm});
            skLineSegment(sketch, "E340", {"start": v(-22, 70.2) * mm, "end": v(-21.96, 70.39) * mm});
            skLineSegment(sketch, "E341", {"start": v(-21.96, 70.39) * mm, "end": v(-21.91, 70.58) * mm});
            skLineSegment(sketch, "E342", {"start": v(-21.91, 70.58) * mm, "end": v(-21.85, 70.77) * mm});
            skLineSegment(sketch, "E343", {"start": v(-21.85, 70.77) * mm, "end": v(-21.76, 70.94) * mm});
            skLineSegment(sketch, "E344", {"start": v(-21.76, 70.94) * mm, "end": v(-21.66, 71.11) * mm});
            skLineSegment(sketch, "E345", {"start": v(-21.66, 71.11) * mm, "end": v(-21.55, 71.27) * mm});
            skLineSegment(sketch, "E346", {"start": v(-21.55, 71.27) * mm, "end": v(-21.41, 71.41) * mm});
            skLineSegment(sketch, "E347", {"start": v(-21.41, 71.41) * mm, "end": v(-21.27, 71.55) * mm});
            skLineSegment(sketch, "E348", {"start": v(-21.27, 71.55) * mm, "end": v(-21.11, 71.66) * mm});
            skLineSegment(sketch, "E349", {"start": v(-21.11, 71.66) * mm, "end": v(-20.94, 71.76) * mm});
            skLineSegment(sketch, "E350", {"start": v(-20.94, 71.76) * mm, "end": v(-20.76, 71.85) * mm});
            skLineSegment(sketch, "E351", {"start": v(-20.76, 71.85) * mm, "end": v(-20.58, 71.91) * mm});
            skLineSegment(sketch, "E352", {"start": v(-20.58, 71.91) * mm, "end": v(-20.39, 71.96) * mm});
            skLineSegment(sketch, "E353", {"start": v(-20.39, 71.96) * mm, "end": v(-20.2, 72) * mm});
            skLineSegment(sketch, "E354", {"start": v(-20.2, 72) * mm, "end": v(-20, 72) * mm});
            skLineSegment(sketch, "E355", {"start": v(-20, 72) * mm, "end": v(-19.8, 72) * mm});
            skLineSegment(sketch, "E356", {"start": v(-19.8, 72) * mm, "end": v(-19.61, 71.96) * mm});
            skLineSegment(sketch, "E357", {"start": v(-19.61, 71.96) * mm, "end": v(-19.42, 71.91) * mm});
            skLineSegment(sketch, "E358", {"start": v(-19.42, 71.91) * mm, "end": v(-19.24, 71.85) * mm});
            skLineSegment(sketch, "E359", {"start": v(-19.24, 71.85) * mm, "end": v(-19.06, 71.76) * mm});
            skLineSegment(sketch, "E360", {"start": v(-19.06, 71.76) * mm, "end": v(-18.89, 71.66) * mm});
            skLineSegment(sketch, "E361", {"start": v(-18.89, 71.66) * mm, "end": v(-18.73, 71.55) * mm});
            skLineSegment(sketch, "E362", {"start": v(-18.73, 71.55) * mm, "end": v(-18.59, 71.41) * mm});
            skLineSegment(sketch, "E363", {"start": v(-18.59, 71.41) * mm, "end": v(-18.45, 71.27) * mm});
            skLineSegment(sketch, "E364", {"start": v(-18.45, 71.27) * mm, "end": v(-18.34, 71.11) * mm});
            skLineSegment(sketch, "E365", {"start": v(-18.34, 71.11) * mm, "end": v(-18.24, 70.94) * mm});
            skLineSegment(sketch, "E366", {"start": v(-18.24, 70.94) * mm, "end": v(-18.15, 70.77) * mm});
            skLineSegment(sketch, "E367", {"start": v(-18.15, 70.77) * mm, "end": v(-18.09, 70.58) * mm});
            skLineSegment(sketch, "E368", {"start": v(-18.09, 70.58) * mm, "end": v(-18.04, 70.39) * mm});
            skLineSegment(sketch, "E369", {"start": v(-18.04, 70.39) * mm, "end": v(-18, 70.2) * mm});
            skLineSegment(sketch, "E370", {"start": v(-18, 70.2) * mm, "end": v(-18, 70) * mm});
            skLineSegment(sketch, "E371", {"start": v(-18, 70) * mm, "end": v(-18, 69.8) * mm});
            skLineSegment(sketch, "E372", {"start": v(-18, 69.8) * mm, "end": v(-18.04, 69.61) * mm});
            skLineSegment(sketch, "E373", {"start": v(-18.04, 69.61) * mm, "end": v(-18.09, 69.42) * mm});
            skLineSegment(sketch, "E374", {"start": v(-18.09, 69.42) * mm, "end": v(-18.15, 69.24) * mm});
            skLineSegment(sketch, "E375", {"start": v(-18.15, 69.24) * mm, "end": v(-18.24, 69.06) * mm});
            skLineSegment(sketch, "E376", {"start": v(-18.24, 69.06) * mm, "end": v(-18.34, 68.89) * mm});
            skLineSegment(sketch, "E377", {"start": v(-18.34, 68.89) * mm, "end": v(-18.45, 68.73) * mm});
            skLineSegment(sketch, "E378", {"start": v(-18.45, 68.73) * mm, "end": v(-18.59, 68.59) * mm});
            skLineSegment(sketch, "E379", {"start": v(-18.59, 68.59) * mm, "end": v(-18.73, 68.45) * mm});
            skLineSegment(sketch, "E380", {"start": v(-18.73, 68.45) * mm, "end": v(-18.89, 68.34) * mm});
            skLineSegment(sketch, "E381", {"start": v(-18.89, 68.34) * mm, "end": v(-19.06, 68.24) * mm});
            skLineSegment(sketch, "E382", {"start": v(-19.06, 68.24) * mm, "end": v(-19.24, 68.15) * mm});
            skLineSegment(sketch, "E383", {"start": v(-19.24, 68.15) * mm, "end": v(-19.42, 68.09) * mm});
            skLineSegment(sketch, "E384", {"start": v(-19.42, 68.09) * mm, "end": v(-19.61, 68.04) * mm});
            skLineSegment(sketch, "E385", {"start": v(-19.61, 68.04) * mm, "end": v(-19.8, 68) * mm});
            skLineSegment(sketch, "E386", {"start": v(-19.8, 68) * mm, "end": v(-20, 68) * mm});
            skLineSegment(sketch, "E387", {"start": v(-20, 68) * mm, "end": v(-20.2, 68) * mm});
            skLineSegment(sketch, "E388", {"start": v(-20.2, 18.01) * mm, "end": v(-20.39, 18.04) * mm});
            skLineSegment(sketch, "E389", {"start": v(-20.39, 18.04) * mm, "end": v(-20.58, 18.09) * mm});
            skLineSegment(sketch, "E390", {"start": v(-20.58, 18.09) * mm, "end": v(-20.76, 18.15) * mm});
            skLineSegment(sketch, "E391", {"start": v(-20.76, 18.15) * mm, "end": v(-20.94, 18.24) * mm});
            skLineSegment(sketch, "E392", {"start": v(-20.94, 18.24) * mm, "end": v(-21.11, 18.34) * mm});
            skLineSegment(sketch, "E393", {"start": v(-21.11, 18.34) * mm, "end": v(-21.27, 18.45) * mm});
            skLineSegment(sketch, "E394", {"start": v(-21.27, 18.45) * mm, "end": v(-21.41, 18.59) * mm});
            skLineSegment(sketch, "E395", {"start": v(-21.41, 18.59) * mm, "end": v(-21.55, 18.73) * mm});
            skLineSegment(sketch, "E396", {"start": v(-21.55, 18.73) * mm, "end": v(-21.66, 18.89) * mm});
            skLineSegment(sketch, "E397", {"start": v(-21.66, 18.89) * mm, "end": v(-21.76, 19.06) * mm});
            skLineSegment(sketch, "E398", {"start": v(-21.76, 19.06) * mm, "end": v(-21.85, 19.23) * mm});
            skLineSegment(sketch, "E399", {"start": v(-21.85, 19.23) * mm, "end": v(-21.91, 19.42) * mm});
            skLineSegment(sketch, "E400", {"start": v(-21.91, 19.42) * mm, "end": v(-21.96, 19.6) * mm});
            skLineSegment(sketch, "E401", {"start": v(-21.96, 19.6) * mm, "end": v(-22, 19.8) * mm});
            skLineSegment(sketch, "E402", {"start": v(-22, 19.8) * mm, "end": v(-22, 20) * mm});
            skLineSegment(sketch, "E403", {"start": v(-22, 20) * mm, "end": v(-22, 20.2) * mm});
            skLineSegment(sketch, "E404", {"start": v(-22, 20.2) * mm, "end": v(-21.96, 20.4) * mm});
            skLineSegment(sketch, "E405", {"start": v(-21.96, 20.4) * mm, "end": v(-21.91, 20.58) * mm});
            skLineSegment(sketch, "E406", {"start": v(-21.91, 20.58) * mm, "end": v(-21.85, 20.77) * mm});
            skLineSegment(sketch, "E407", {"start": v(-21.85, 20.77) * mm, "end": v(-21.76, 20.94) * mm});
            skLineSegment(sketch, "E408", {"start": v(-21.76, 20.94) * mm, "end": v(-21.66, 21.11) * mm});
            skLineSegment(sketch, "E409", {"start": v(-21.66, 21.11) * mm, "end": v(-21.55, 21.27) * mm});
            skLineSegment(sketch, "E410", {"start": v(-21.55, 21.27) * mm, "end": v(-21.41, 21.41) * mm});
            skLineSegment(sketch, "E411", {"start": v(-21.41, 21.41) * mm, "end": v(-21.27, 21.55) * mm});
            skLineSegment(sketch, "E412", {"start": v(-21.27, 21.55) * mm, "end": v(-21.11, 21.66) * mm});
            skLineSegment(sketch, "E413", {"start": v(-21.11, 21.66) * mm, "end": v(-20.94, 21.76) * mm});
            skLineSegment(sketch, "E414", {"start": v(-20.94, 21.76) * mm, "end": v(-20.76, 21.85) * mm});
            skLineSegment(sketch, "E415", {"start": v(-20.76, 21.85) * mm, "end": v(-20.58, 21.91) * mm});
            skLineSegment(sketch, "E416", {"start": v(-20.58, 21.91) * mm, "end": v(-20.39, 21.96) * mm});
            skLineSegment(sketch, "E417", {"start": v(-20.39, 21.96) * mm, "end": v(-20.2, 21.99) * mm});
            skLineSegment(sketch, "E418", {"start": v(-20.2, 21.99) * mm, "end": v(-20, 22) * mm});
            skLineSegment(sketch, "E419", {"start": v(-20, 22) * mm, "end": v(-19.8, 21.99) * mm});
            skLineSegment(sketch, "E420", {"start": v(-19.8, 21.99) * mm, "end": v(-19.61, 21.96) * mm});
            skLineSegment(sketch, "E421", {"start": v(-19.61, 21.96) * mm, "end": v(-19.42, 21.91) * mm});
            skLineSegment(sketch, "E422", {"start": v(-19.42, 21.91) * mm, "end": v(-19.24, 21.85) * mm});
            skLineSegment(sketch, "E423", {"start": v(-19.24, 21.85) * mm, "end": v(-19.06, 21.76) * mm});
            skLineSegment(sketch, "E424", {"start": v(-19.06, 21.76) * mm, "end": v(-18.89, 21.66) * mm});
            skLineSegment(sketch, "E425", {"start": v(-18.89, 21.66) * mm, "end": v(-18.73, 21.55) * mm});
            skLineSegment(sketch, "E426", {"start": v(-18.73, 21.55) * mm, "end": v(-18.59, 21.41) * mm});
            skLineSegment(sketch, "E427", {"start": v(-18.59, 21.41) * mm, "end": v(-18.45, 21.27) * mm});
            skLineSegment(sketch, "E428", {"start": v(-18.45, 21.27) * mm, "end": v(-18.34, 21.11) * mm});
            skLineSegment(sketch, "E429", {"start": v(-18.34, 21.11) * mm, "end": v(-18.24, 20.94) * mm});
            skLineSegment(sketch, "E430", {"start": v(-18.24, 20.94) * mm, "end": v(-18.15, 20.77) * mm});
            skLineSegment(sketch, "E431", {"start": v(-18.15, 20.77) * mm, "end": v(-18.09, 20.58) * mm});
            skLineSegment(sketch, "E432", {"start": v(-18.09, 20.58) * mm, "end": v(-18.04, 20.4) * mm});
            skLineSegment(sketch, "E433", {"start": v(-18.04, 20.4) * mm, "end": v(-18, 20.2) * mm});
            skLineSegment(sketch, "E434", {"start": v(-18, 20.2) * mm, "end": v(-18, 20) * mm});
            skLineSegment(sketch, "E435", {"start": v(-18, 20) * mm, "end": v(-18, 19.8) * mm});
            skLineSegment(sketch, "E436", {"start": v(-18, 19.8) * mm, "end": v(-18.04, 19.6) * mm});
            skLineSegment(sketch, "E437", {"start": v(-18.04, 19.6) * mm, "end": v(-18.09, 19.42) * mm});
            skLineSegment(sketch, "E438", {"start": v(-18.09, 19.42) * mm, "end": v(-18.15, 19.23) * mm});
            skLineSegment(sketch, "E439", {"start": v(-18.15, 19.23) * mm, "end": v(-18.24, 19.06) * mm});
            skLineSegment(sketch, "E440", {"start": v(-18.24, 19.06) * mm, "end": v(-18.34, 18.89) * mm});
            skLineSegment(sketch, "E441", {"start": v(-18.34, 18.89) * mm, "end": v(-18.45, 18.73) * mm});
            skLineSegment(sketch, "E442", {"start": v(-18.45, 18.73) * mm, "end": v(-18.59, 18.59) * mm});
            skLineSegment(sketch, "E443", {"start": v(-18.59, 18.59) * mm, "end": v(-18.73, 18.45) * mm});
            skLineSegment(sketch, "E444", {"start": v(-18.73, 18.45) * mm, "end": v(-18.89, 18.34) * mm});
            skLineSegment(sketch, "E445", {"start": v(-18.89, 18.34) * mm, "end": v(-19.06, 18.24) * mm});
            skLineSegment(sketch, "E446", {"start": v(-19.06, 18.24) * mm, "end": v(-19.24, 18.15) * mm});
            skLineSegment(sketch, "E447", {"start": v(-19.24, 18.15) * mm, "end": v(-19.42, 18.09) * mm});
            skLineSegment(sketch, "E448", {"start": v(-19.42, 18.09) * mm, "end": v(-19.61, 18.04) * mm});
            skLineSegment(sketch, "E449", {"start": v(-19.61, 18.04) * mm, "end": v(-19.8, 18.01) * mm});
            skLineSegment(sketch, "E450", {"start": v(-19.8, 18.01) * mm, "end": v(-20, 18) * mm});
            skLineSegment(sketch, "E451", {"start": v(-20, 18) * mm, "end": v(-20.2, 18.01) * mm});
            skLineSegment(sketch, "E452", {"start": v(-40.25, -12.49) * mm, "end": v(-40.49, -12.45) * mm});
            skLineSegment(sketch, "E453", {"start": v(-40.49, -12.45) * mm, "end": v(-40.73, -12.4) * mm});
            skLineSegment(sketch, "E454", {"start": v(-40.73, -12.4) * mm, "end": v(-40.96, -12.3) * mm});
            skLineSegment(sketch, "E455", {"start": v(-40.96, -12.3) * mm, "end": v(-41.18, -12.2) * mm});
            skLineSegment(sketch, "E456", {"start": v(-41.18, -12.2) * mm, "end": v(-41.39, -12.08) * mm});
            skLineSegment(sketch, "E457", {"start": v(-41.39, -12.08) * mm, "end": v(-41.59, -11.93) * mm});
            skLineSegment(sketch, "E458", {"start": v(-41.59, -11.93) * mm, "end": v(-41.77, -11.77) * mm});
            skLineSegment(sketch, "E459", {"start": v(-41.77, -11.77) * mm, "end": v(-41.93, -11.59) * mm});
            skLineSegment(sketch, "E460", {"start": v(-41.93, -11.59) * mm, "end": v(-42.08, -11.39) * mm});
            skLineSegment(sketch, "E461", {"start": v(-42.08, -11.39) * mm, "end": v(-42.2, -11.18) * mm});
            skLineSegment(sketch, "E462", {"start": v(-42.2, -11.18) * mm, "end": v(-42.31, -10.96) * mm});
            skLineSegment(sketch, "E463", {"start": v(-42.31, -10.96) * mm, "end": v(-42.4, -10.73) * mm});
            skLineSegment(sketch, "E464", {"start": v(-42.4, -10.73) * mm, "end": v(-42.45, -10.49) * mm});
            skLineSegment(sketch, "E465", {"start": v(-42.45, -10.49) * mm, "end": v(-42.49, -10.25) * mm});
            skLineSegment(sketch, "E466", {"start": v(-42.49, -10.25) * mm, "end": v(-42.5, -10) * mm});
            skLineSegment(sketch, "E467", {"start": v(-42.5, -10) * mm, "end": v(-42.49, -9.75) * mm});
            skLineSegment(sketch, "E468", {"start": v(-42.49, -9.75) * mm, "end": v(-42.45, -9.51) * mm});
            skLineSegment(sketch, "E469", {"start": v(-42.45, -9.51) * mm, "end": v(-42.4, -9.27) * mm});
            skLineSegment(sketch, "E470", {"start": v(-42.4, -9.27) * mm, "end": v(-42.31, -9.04) * mm});
            skLineSegment(sketch, "E471", {"start": v(-42.31, -9.04) * mm, "end": v(-42.2, -8.82) * mm});
            skLineSegment(sketch, "E472", {"start": v(-42.2, -8.82) * mm, "end": v(-42.08, -8.61) * mm});
            skLineSegment(sketch, "E473", {"start": v(-42.08, -8.61) * mm, "end": v(-41.93, -8.41) * mm});
            skLineSegment(sketch, "E474", {"start": v(-41.93, -8.41) * mm, "end": v(-41.77, -8.23) * mm});
            skLineSegment(sketch, "E475", {"start": v(-41.77, -8.23) * mm, "end": v(-41.59, -8.07) * mm});
            skLineSegment(sketch, "E476", {"start": v(-41.59, -8.07) * mm, "end": v(-41.39, -7.92) * mm});
            skLineSegment(sketch, "E477", {"start": v(-41.39, -7.92) * mm, "end": v(-41.18, -7.8) * mm});
            skLineSegment(sketch, "E478", {"start": v(-41.18, -7.8) * mm, "end": v(-40.96, -7.7) * mm});
            skLineSegment(sketch, "E479", {"start": v(-40.96, -7.7) * mm, "end": v(-40.73, -7.6) * mm});
            skLineSegment(sketch, "E480", {"start": v(-40.73, -7.6) * mm, "end": v(-40.49, -7.55) * mm});
            skLineSegment(sketch, "E481", {"start": v(-40.49, -7.55) * mm, "end": v(-40.25, -7.51) * mm});
            skLineSegment(sketch, "E482", {"start": v(-40.25, -7.51) * mm, "end": v(-40, -7.5) * mm});
            skLineSegment(sketch, "E483", {"start": v(-40, -7.5) * mm, "end": v(-39.75, -7.51) * mm});
            skLineSegment(sketch, "E484", {"start": v(-39.75, -7.51) * mm, "end": v(-39.51, -7.55) * mm});
            skLineSegment(sketch, "E485", {"start": v(-39.51, -7.55) * mm, "end": v(-39.27, -7.6) * mm});
            skLineSegment(sketch, "E486", {"start": v(-39.27, -7.6) * mm, "end": v(-39.04, -7.7) * mm});
            skLineSegment(sketch, "E487", {"start": v(-39.04, -7.7) * mm, "end": v(-38.82, -7.8) * mm});
            skLineSegment(sketch, "E488", {"start": v(-38.82, -7.8) * mm, "end": v(-38.61, -7.92) * mm});
            skLineSegment(sketch, "E489", {"start": v(-38.61, -7.92) * mm, "end": v(-38.41, -8.07) * mm});
            skLineSegment(sketch, "E490", {"start": v(-38.41, -8.07) * mm, "end": v(-38.23, -8.23) * mm});
            skLineSegment(sketch, "E491", {"start": v(-38.23, -8.23) * mm, "end": v(-38.07, -8.41) * mm});
            skLineSegment(sketch, "E492", {"start": v(-38.07, -8.41) * mm, "end": v(-37.92, -8.61) * mm});
            skLineSegment(sketch, "E493", {"start": v(-37.92, -8.61) * mm, "end": v(-37.8, -8.82) * mm});
            skLineSegment(sketch, "E494", {"start": v(-37.8, -8.82) * mm, "end": v(-37.69, -9.04) * mm});
            skLineSegment(sketch, "E495", {"start": v(-37.69, -9.04) * mm, "end": v(-37.6, -9.27) * mm});
            skLineSegment(sketch, "E496", {"start": v(-37.6, -9.27) * mm, "end": v(-37.55, -9.51) * mm});
            skLineSegment(sketch, "E497", {"start": v(-37.55, -9.51) * mm, "end": v(-37.51, -9.75) * mm});
            skLineSegment(sketch, "E498", {"start": v(-37.51, -9.75) * mm, "end": v(-37.5, -10) * mm});
            skLineSegment(sketch, "E499", {"start": v(-37.5, -10) * mm, "end": v(-37.51, -10.25) * mm});
            skLineSegment(sketch, "E500", {"start": v(-37.51, -10.25) * mm, "end": v(-37.55, -10.49) * mm});
            skLineSegment(sketch, "E501", {"start": v(-37.55, -10.49) * mm, "end": v(-37.6, -10.73) * mm});
            skLineSegment(sketch, "E502", {"start": v(-37.6, -10.73) * mm, "end": v(-37.69, -10.96) * mm});
            skLineSegment(sketch, "E503", {"start": v(-37.69, -10.96) * mm, "end": v(-37.8, -11.18) * mm});
            skLineSegment(sketch, "E504", {"start": v(-37.8, -11.18) * mm, "end": v(-37.92, -11.39) * mm});
            skLineSegment(sketch, "E505", {"start": v(-37.92, -11.39) * mm, "end": v(-38.07, -11.59) * mm});
            skLineSegment(sketch, "E506", {"start": v(-38.07, -11.59) * mm, "end": v(-38.23, -11.77) * mm});
            skLineSegment(sketch, "E507", {"start": v(-38.23, -11.77) * mm, "end": v(-38.41, -11.93) * mm});
            skLineSegment(sketch, "E508", {"start": v(-38.41, -11.93) * mm, "end": v(-38.61, -12.08) * mm});
            skLineSegment(sketch, "E509", {"start": v(-38.61, -12.08) * mm, "end": v(-38.82, -12.2) * mm});
            skLineSegment(sketch, "E510", {"start": v(-38.82, -12.2) * mm, "end": v(-39.04, -12.3) * mm});
            skLineSegment(sketch, "E511", {"start": v(-39.04, -12.3) * mm, "end": v(-39.27, -12.4) * mm});
            skLineSegment(sketch, "E512", {"start": v(-39.27, -12.4) * mm, "end": v(-39.51, -12.45) * mm});
            skLineSegment(sketch, "E513", {"start": v(-39.51, -12.45) * mm, "end": v(-39.75, -12.49) * mm});
            skLineSegment(sketch, "E514", {"start": v(-39.75, -12.49) * mm, "end": v(-40, -12.5) * mm});
            skLineSegment(sketch, "E515", {"start": v(-40, -12.5) * mm, "end": v(-40.25, -12.49) * mm});
            skLineSegment(sketch, "E516", {"start": v(81.85, -23.54) * mm, "end": v(81.7, -23.52) * mm});
            skLineSegment(sketch, "E517", {"start": v(81.7, -23.52) * mm, "end": v(81.55, -23.48) * mm});
            skLineSegment(sketch, "E518", {"start": v(81.55, -23.48) * mm, "end": v(81.4, -23.43) * mm});
            skLineSegment(sketch, "E519", {"start": v(81.4, -23.43) * mm, "end": v(81.27, -23.37) * mm});
            skLineSegment(sketch, "E520", {"start": v(81.27, -23.37) * mm, "end": v(81.14, -23.29) * mm});
            skLineSegment(sketch, "E521", {"start": v(81.14, -23.29) * mm, "end": v(81.02, -23.2) * mm});
            skLineSegment(sketch, "E522", {"start": v(81.02, -23.2) * mm, "end": v(80.9, -23.1) * mm});
            skLineSegment(sketch, "E523", {"start": v(80.9, -23.1) * mm, "end": v(80.8, -22.98) * mm});
            skLineSegment(sketch, "E524", {"start": v(80.8, -22.98) * mm, "end": v(80.71, -22.86) * mm});
            skLineSegment(sketch, "E525", {"start": v(80.71, -22.86) * mm, "end": v(80.63, -22.73) * mm});
            skLineSegment(sketch, "E526", {"start": v(80.63, -22.73) * mm, "end": v(80.57, -22.6) * mm});
            skLineSegment(sketch, "E527", {"start": v(80.57, -22.6) * mm, "end": v(80.52, -22.45) * mm});
            skLineSegment(sketch, "E528", {"start": v(80.52, -22.45) * mm, "end": v(80.48, -22.3) * mm});
            skLineSegment(sketch, "E529", {"start": v(80.48, -22.3) * mm, "end": v(80.46, -22.15) * mm});
            skLineSegment(sketch, "E530", {"start": v(80.46, -22.15) * mm, "end": v(80.45, -22) * mm});
            skLineSegment(sketch, "E531", {"start": v(80.45, -22) * mm, "end": v(80.46, -21.85) * mm});
            skLineSegment(sketch, "E532", {"start": v(80.46, -21.85) * mm, "end": v(80.48, -21.7) * mm});
            skLineSegment(sketch, "E533", {"start": v(80.48, -21.7) * mm, "end": v(80.52, -21.55) * mm});
            skLineSegment(sketch, "E534", {"start": v(80.52, -21.55) * mm, "end": v(80.57, -21.4) * mm});
            skLineSegment(sketch, "E535", {"start": v(80.57, -21.4) * mm, "end": v(80.63, -21.27) * mm});
            skLineSegment(sketch, "E536", {"start": v(80.63, -21.27) * mm, "end": v(80.71, -21.14) * mm});
            skLineSegment(sketch, "E537", {"start": v(80.71, -21.14) * mm, "end": v(80.8, -21.02) * mm});
            skLineSegment(sketch, "E538", {"start": v(80.8, -21.02) * mm, "end": v(80.9, -20.9) * mm});
            skLineSegment(sketch, "E539", {"start": v(80.9, -20.9) * mm, "end": v(81.02, -20.8) * mm});
            skLineSegment(sketch, "E540", {"start": v(81.02, -20.8) * mm, "end": v(81.14, -20.71) * mm});
            skLineSegment(sketch, "E541", {"start": v(81.14, -20.71) * mm, "end": v(81.27, -20.63) * mm});
            skLineSegment(sketch, "E542", {"start": v(81.27, -20.63) * mm, "end": v(81.4, -20.57) * mm});
            skLineSegment(sketch, "E543", {"start": v(81.4, -20.57) * mm, "end": v(81.55, -20.52) * mm});
            skLineSegment(sketch, "E544", {"start": v(81.55, -20.52) * mm, "end": v(81.7, -20.48) * mm});
            skLineSegment(sketch, "E545", {"start": v(81.7, -20.48) * mm, "end": v(81.85, -20.46) * mm});
            skLineSegment(sketch, "E546", {"start": v(81.85, -20.46) * mm, "end": v(82, -20.45) * mm});
            skLineSegment(sketch, "E547", {"start": v(82, -20.45) * mm, "end": v(82.15, -20.46) * mm});
            skLineSegment(sketch, "E548", {"start": v(82.15, -20.46) * mm, "end": v(82.3, -20.48) * mm});
            skLineSegment(sketch, "E549", {"start": v(82.3, -20.48) * mm, "end": v(82.45, -20.52) * mm});
            skLineSegment(sketch, "E550", {"start": v(82.45, -20.52) * mm, "end": v(82.6, -20.57) * mm});
            skLineSegment(sketch, "E551", {"start": v(82.6, -20.57) * mm, "end": v(82.73, -20.63) * mm});
            skLineSegment(sketch, "E552", {"start": v(82.73, -20.63) * mm, "end": v(82.86, -20.71) * mm});
            skLineSegment(sketch, "E553", {"start": v(82.86, -20.71) * mm, "end": v(82.98, -20.8) * mm});
            skLineSegment(sketch, "E554", {"start": v(82.98, -20.8) * mm, "end": v(83.1, -20.9) * mm});
            skLineSegment(sketch, "E555", {"start": v(83.1, -20.9) * mm, "end": v(83.2, -21.02) * mm});
            skLineSegment(sketch, "E556", {"start": v(83.2, -21.02) * mm, "end": v(83.29, -21.14) * mm});
            skLineSegment(sketch, "E557", {"start": v(83.29, -21.14) * mm, "end": v(83.37, -21.27) * mm});
            skLineSegment(sketch, "E558", {"start": v(83.37, -21.27) * mm, "end": v(83.43, -21.4) * mm});
            skLineSegment(sketch, "E559", {"start": v(83.43, -21.4) * mm, "end": v(83.48, -21.55) * mm});
            skLineSegment(sketch, "E560", {"start": v(83.48, -21.55) * mm, "end": v(83.52, -21.7) * mm});
            skLineSegment(sketch, "E561", {"start": v(83.52, -21.7) * mm, "end": v(83.54, -21.85) * mm});
            skLineSegment(sketch, "E562", {"start": v(83.54, -21.85) * mm, "end": v(83.55, -22) * mm});
            skLineSegment(sketch, "E563", {"start": v(83.55, -22) * mm, "end": v(83.54, -22.15) * mm});
            skLineSegment(sketch, "E564", {"start": v(83.54, -22.15) * mm, "end": v(83.52, -22.3) * mm});
            skLineSegment(sketch, "E565", {"start": v(83.52, -22.3) * mm, "end": v(83.48, -22.45) * mm});
            skLineSegment(sketch, "E566", {"start": v(83.48, -22.45) * mm, "end": v(83.43, -22.6) * mm});
            skLineSegment(sketch, "E567", {"start": v(83.43, -22.6) * mm, "end": v(83.37, -22.73) * mm});
            skLineSegment(sketch, "E568", {"start": v(83.37, -22.73) * mm, "end": v(83.29, -22.86) * mm});
            skLineSegment(sketch, "E569", {"start": v(83.29, -22.86) * mm, "end": v(83.2, -22.98) * mm});
            skLineSegment(sketch, "E570", {"start": v(83.2, -22.98) * mm, "end": v(83.1, -23.1) * mm});
            skLineSegment(sketch, "E571", {"start": v(83.1, -23.1) * mm, "end": v(82.98, -23.2) * mm});
            skLineSegment(sketch, "E572", {"start": v(82.98, -23.2) * mm, "end": v(82.86, -23.29) * mm});
            skLineSegment(sketch, "E573", {"start": v(82.86, -23.29) * mm, "end": v(82.73, -23.37) * mm});
            skLineSegment(sketch, "E574", {"start": v(82.73, -23.37) * mm, "end": v(82.6, -23.43) * mm});
            skLineSegment(sketch, "E575", {"start": v(82.6, -23.43) * mm, "end": v(82.45, -23.48) * mm});
            skLineSegment(sketch, "E576", {"start": v(82.45, -23.48) * mm, "end": v(82.3, -23.52) * mm});
            skLineSegment(sketch, "E577", {"start": v(82.3, -23.52) * mm, "end": v(82.15, -23.54) * mm});
            skLineSegment(sketch, "E578", {"start": v(82.15, -23.54) * mm, "end": v(82, -23.55) * mm});
            skLineSegment(sketch, "E579", {"start": v(82, -23.55) * mm, "end": v(81.85, -23.54) * mm});
            skLineSegment(sketch, "E580", {"start": v(-40.25, -32.49) * mm, "end": v(-40.49, -32.45) * mm});
            skLineSegment(sketch, "E581", {"start": v(-40.49, -32.45) * mm, "end": v(-40.73, -32.4) * mm});
            skLineSegment(sketch, "E582", {"start": v(-40.73, -32.4) * mm, "end": v(-40.96, -32.3) * mm});
            skLineSegment(sketch, "E583", {"start": v(-40.96, -32.3) * mm, "end": v(-41.18, -32.2) * mm});
            skLineSegment(sketch, "E584", {"start": v(-41.18, -32.2) * mm, "end": v(-41.39, -32.08) * mm});
            skLineSegment(sketch, "E585", {"start": v(-41.39, -32.08) * mm, "end": v(-41.59, -31.93) * mm});
            skLineSegment(sketch, "E586", {"start": v(-41.59, -31.93) * mm, "end": v(-41.77, -31.77) * mm});
            skLineSegment(sketch, "E587", {"start": v(-41.77, -31.77) * mm, "end": v(-41.93, -31.59) * mm});
            skLineSegment(sketch, "E588", {"start": v(-41.93, -31.59) * mm, "end": v(-42.08, -31.39) * mm});
            skLineSegment(sketch, "E589", {"start": v(-42.08, -31.39) * mm, "end": v(-42.2, -31.18) * mm});
            skLineSegment(sketch, "E590", {"start": v(-42.2, -31.18) * mm, "end": v(-42.31, -30.96) * mm});
            skLineSegment(sketch, "E591", {"start": v(-42.31, -30.96) * mm, "end": v(-42.4, -30.73) * mm});
            skLineSegment(sketch, "E592", {"start": v(-42.4, -30.73) * mm, "end": v(-42.45, -30.49) * mm});
            skLineSegment(sketch, "E593", {"start": v(-42.45, -30.49) * mm, "end": v(-42.49, -30.25) * mm});
            skLineSegment(sketch, "E594", {"start": v(-42.49, -30.25) * mm, "end": v(-42.5, -30) * mm});
            skLineSegment(sketch, "E595", {"start": v(-42.5, -30) * mm, "end": v(-42.49, -29.75) * mm});
            skLineSegment(sketch, "E596", {"start": v(-42.49, -29.75) * mm, "end": v(-42.45, -29.51) * mm});
            skLineSegment(sketch, "E597", {"start": v(-42.45, -29.51) * mm, "end": v(-42.4, -29.27) * mm});
            skLineSegment(sketch, "E598", {"start": v(-42.4, -29.27) * mm, "end": v(-42.31, -29.04) * mm});
            skLineSegment(sketch, "E599", {"start": v(-42.31, -29.04) * mm, "end": v(-42.2, -28.82) * mm});
            skLineSegment(sketch, "E600", {"start": v(-42.2, -28.82) * mm, "end": v(-42.08, -28.61) * mm});
            skLineSegment(sketch, "E601", {"start": v(-42.08, -28.61) * mm, "end": v(-41.93, -28.41) * mm});
            skLineSegment(sketch, "E602", {"start": v(-41.93, -28.41) * mm, "end": v(-41.77, -28.23) * mm});
            skLineSegment(sketch, "E603", {"start": v(-41.77, -28.23) * mm, "end": v(-41.59, -28.07) * mm});
            skLineSegment(sketch, "E604", {"start": v(-41.59, -28.07) * mm, "end": v(-41.39, -27.92) * mm});
            skLineSegment(sketch, "E605", {"start": v(-41.39, -27.92) * mm, "end": v(-41.18, -27.8) * mm});
            skLineSegment(sketch, "E606", {"start": v(-41.18, -27.8) * mm, "end": v(-40.96, -27.7) * mm});
            skLineSegment(sketch, "E607", {"start": v(-40.96, -27.7) * mm, "end": v(-40.73, -27.6) * mm});
            skLineSegment(sketch, "E608", {"start": v(-40.73, -27.6) * mm, "end": v(-40.49, -27.55) * mm});
            skLineSegment(sketch, "E609", {"start": v(-40.49, -27.55) * mm, "end": v(-40.25, -27.51) * mm});
            skLineSegment(sketch, "E610", {"start": v(-40.25, -27.51) * mm, "end": v(-40, -27.5) * mm});
            skLineSegment(sketch, "E611", {"start": v(-40, -27.5) * mm, "end": v(-39.75, -27.51) * mm});
            skLineSegment(sketch, "E612", {"start": v(-39.75, -27.51) * mm, "end": v(-39.51, -27.55) * mm});
            skLineSegment(sketch, "E613", {"start": v(-39.51, -27.55) * mm, "end": v(-39.27, -27.6) * mm});
            skLineSegment(sketch, "E614", {"start": v(-39.27, -27.6) * mm, "end": v(-39.04, -27.7) * mm});
            skLineSegment(sketch, "E615", {"start": v(-39.04, -27.7) * mm, "end": v(-38.82, -27.8) * mm});
            skLineSegment(sketch, "E616", {"start": v(-38.82, -27.8) * mm, "end": v(-38.61, -27.92) * mm});
            skLineSegment(sketch, "E617", {"start": v(-38.61, -27.92) * mm, "end": v(-38.41, -28.07) * mm});
            skLineSegment(sketch, "E618", {"start": v(-38.41, -28.07) * mm, "end": v(-38.23, -28.23) * mm});
            skLineSegment(sketch, "E619", {"start": v(-38.23, -28.23) * mm, "end": v(-38.07, -28.41) * mm});
            skLineSegment(sketch, "E620", {"start": v(-38.07, -28.41) * mm, "end": v(-37.92, -28.61) * mm});
            skLineSegment(sketch, "E621", {"start": v(-37.92, -28.61) * mm, "end": v(-37.8, -28.82) * mm});
            skLineSegment(sketch, "E622", {"start": v(-37.8, -28.82) * mm, "end": v(-37.69, -29.04) * mm});
            skLineSegment(sketch, "E623", {"start": v(-37.69, -29.04) * mm, "end": v(-37.6, -29.27) * mm});
            skLineSegment(sketch, "E624", {"start": v(-37.6, -29.27) * mm, "end": v(-37.55, -29.51) * mm});
            skLineSegment(sketch, "E625", {"start": v(-37.55, -29.51) * mm, "end": v(-37.51, -29.75) * mm});
            skLineSegment(sketch, "E626", {"start": v(-37.51, -29.75) * mm, "end": v(-37.5, -30) * mm});
            skLineSegment(sketch, "E627", {"start": v(-37.5, -30) * mm, "end": v(-37.51, -30.25) * mm});
            skLineSegment(sketch, "E628", {"start": v(-37.51, -30.25) * mm, "end": v(-37.55, -30.49) * mm});
            skLineSegment(sketch, "E629", {"start": v(-37.55, -30.49) * mm, "end": v(-37.6, -30.73) * mm});
            skLineSegment(sketch, "E630", {"start": v(-37.6, -30.73) * mm, "end": v(-37.69, -30.96) * mm});
            skLineSegment(sketch, "E631", {"start": v(-37.69, -30.96) * mm, "end": v(-37.8, -31.18) * mm});
            skLineSegment(sketch, "E632", {"start": v(-37.8, -31.18) * mm, "end": v(-37.92, -31.39) * mm});
            skLineSegment(sketch, "E633", {"start": v(-37.92, -31.39) * mm, "end": v(-38.07, -31.59) * mm});
            skLineSegment(sketch, "E634", {"start": v(-38.07, -31.59) * mm, "end": v(-38.23, -31.77) * mm});
            skLineSegment(sketch, "E635", {"start": v(-38.23, -31.77) * mm, "end": v(-38.41, -31.93) * mm});
            skLineSegment(sketch, "E636", {"start": v(-38.41, -31.93) * mm, "end": v(-38.61, -32.08) * mm});
            skLineSegment(sketch, "E637", {"start": v(-38.61, -32.08) * mm, "end": v(-38.82, -32.2) * mm});
            skLineSegment(sketch, "E638", {"start": v(-38.82, -32.2) * mm, "end": v(-39.04, -32.3) * mm});
            skLineSegment(sketch, "E639", {"start": v(-39.04, -32.3) * mm, "end": v(-39.27, -32.4) * mm});
            skLineSegment(sketch, "E640", {"start": v(-39.27, -32.4) * mm, "end": v(-39.51, -32.45) * mm});
            skLineSegment(sketch, "E641", {"start": v(-39.51, -32.45) * mm, "end": v(-39.75, -32.49) * mm});
            skLineSegment(sketch, "E642", {"start": v(-39.75, -32.49) * mm, "end": v(-40, -32.5) * mm});
            skLineSegment(sketch, "E643", {"start": v(-40, -32.5) * mm, "end": v(-40.25, -32.49) * mm});
            skLineSegment(sketch, "E644", {"start": v(-20.2, -32) * mm, "end": v(-20.39, -31.96) * mm});
            skLineSegment(sketch, "E645", {"start": v(-20.39, -31.96) * mm, "end": v(-20.58, -31.91) * mm});
            skLineSegment(sketch, "E646", {"start": v(-20.58, -31.91) * mm, "end": v(-20.76, -31.85) * mm});
            skLineSegment(sketch, "E647", {"start": v(-20.76, -31.85) * mm, "end": v(-20.94, -31.76) * mm});
            skLineSegment(sketch, "E648", {"start": v(-20.94, -31.76) * mm, "end": v(-21.11, -31.66) * mm});
            skLineSegment(sketch, "E649", {"start": v(-21.11, -31.66) * mm, "end": v(-21.27, -31.55) * mm});
            skLineSegment(sketch, "E650", {"start": v(-21.27, -31.55) * mm, "end": v(-21.41, -31.41) * mm});
            skLineSegment(sketch, "E651", {"start": v(-21.41, -31.41) * mm, "end": v(-21.55, -31.27) * mm});
            skLineSegment(sketch, "E652", {"start": v(-21.55, -31.27) * mm, "end": v(-21.66, -31.11) * mm});
            skLineSegment(sketch, "E653", {"start": v(-21.66, -31.11) * mm, "end": v(-21.76, -30.94) * mm});
            skLineSegment(sketch, "E654", {"start": v(-21.76, -30.94) * mm, "end": v(-21.85, -30.77) * mm});
            skLineSegment(sketch, "E655", {"start": v(-21.85, -30.77) * mm, "end": v(-21.91, -30.58) * mm});
            skLineSegment(sketch, "E656", {"start": v(-21.91, -30.58) * mm, "end": v(-21.96, -30.4) * mm});
            skLineSegment(sketch, "E657", {"start": v(-21.96, -30.4) * mm, "end": v(-22, -30.2) * mm});
            skLineSegment(sketch, "E658", {"start": v(-22, -30.2) * mm, "end": v(-22, -30) * mm});
            skLineSegment(sketch, "E659", {"start": v(-22, -30) * mm, "end": v(-22, -29.8) * mm});
            skLineSegment(sketch, "E660", {"start": v(-22, -29.8) * mm, "end": v(-21.96, -29.6) * mm});
            skLineSegment(sketch, "E661", {"start": v(-21.96, -29.6) * mm, "end": v(-21.91, -29.42) * mm});
            skLineSegment(sketch, "E662", {"start": v(-21.91, -29.42) * mm, "end": v(-21.85, -29.23) * mm});
            skLineSegment(sketch, "E663", {"start": v(-21.85, -29.23) * mm, "end": v(-21.76, -29.06) * mm});
            skLineSegment(sketch, "E664", {"start": v(-21.76, -29.06) * mm, "end": v(-21.66, -28.89) * mm});
            skLineSegment(sketch, "E665", {"start": v(-21.66, -28.89) * mm, "end": v(-21.55, -28.73) * mm});
            skLineSegment(sketch, "E666", {"start": v(-21.55, -28.73) * mm, "end": v(-21.41, -28.59) * mm});
            skLineSegment(sketch, "E667", {"start": v(-21.41, -28.59) * mm, "end": v(-21.27, -28.45) * mm});
            skLineSegment(sketch, "E668", {"start": v(-21.27, -28.45) * mm, "end": v(-21.11, -28.34) * mm});
            skLineSegment(sketch, "E669", {"start": v(-21.11, -28.34) * mm, "end": v(-20.94, -28.24) * mm});
            skLineSegment(sketch, "E670", {"start": v(-20.94, -28.24) * mm, "end": v(-20.76, -28.15) * mm});
            skLineSegment(sketch, "E671", {"start": v(-20.76, -28.15) * mm, "end": v(-20.58, -28.09) * mm});
            skLineSegment(sketch, "E672", {"start": v(-20.58, -28.09) * mm, "end": v(-20.39, -28.04) * mm});
            skLineSegment(sketch, "E673", {"start": v(-20.39, -28.04) * mm, "end": v(-20.2, -28) * mm});
            skLineSegment(sketch, "E674", {"start": v(-20.2, -28) * mm, "end": v(-20, -28) * mm});
            skLineSegment(sketch, "E675", {"start": v(-20, -28) * mm, "end": v(-19.8, -28) * mm});
            skLineSegment(sketch, "E676", {"start": v(-19.8, -28) * mm, "end": v(-19.61, -28.04) * mm});
            skLineSegment(sketch, "E677", {"start": v(-19.61, -28.04) * mm, "end": v(-19.42, -28.09) * mm});
            skLineSegment(sketch, "E678", {"start": v(-19.42, -28.09) * mm, "end": v(-19.24, -28.15) * mm});
            skLineSegment(sketch, "E679", {"start": v(-19.24, -28.15) * mm, "end": v(-19.06, -28.24) * mm});
            skLineSegment(sketch, "E680", {"start": v(-19.06, -28.24) * mm, "end": v(-18.89, -28.34) * mm});
            skLineSegment(sketch, "E681", {"start": v(-18.89, -28.34) * mm, "end": v(-18.73, -28.45) * mm});
            skLineSegment(sketch, "E682", {"start": v(-18.73, -28.45) * mm, "end": v(-18.59, -28.59) * mm});
            skLineSegment(sketch, "E683", {"start": v(-18.59, -28.59) * mm, "end": v(-18.45, -28.73) * mm});
            skLineSegment(sketch, "E684", {"start": v(-18.45, -28.73) * mm, "end": v(-18.34, -28.89) * mm});
            skLineSegment(sketch, "E685", {"start": v(-18.34, -28.89) * mm, "end": v(-18.24, -29.06) * mm});
            skLineSegment(sketch, "E686", {"start": v(-18.24, -29.06) * mm, "end": v(-18.15, -29.23) * mm});
            skLineSegment(sketch, "E687", {"start": v(-18.15, -29.23) * mm, "end": v(-18.09, -29.42) * mm});
            skLineSegment(sketch, "E688", {"start": v(-18.09, -29.42) * mm, "end": v(-18.04, -29.6) * mm});
            skLineSegment(sketch, "E689", {"start": v(-18.04, -29.6) * mm, "end": v(-18, -29.8) * mm});
            skLineSegment(sketch, "E690", {"start": v(-18, -29.8) * mm, "end": v(-18, -30) * mm});
            skLineSegment(sketch, "E691", {"start": v(-18, -30) * mm, "end": v(-18, -30.2) * mm});
            skLineSegment(sketch, "E692", {"start": v(-18, -30.2) * mm, "end": v(-18.04, -30.4) * mm});
            skLineSegment(sketch, "E693", {"start": v(-18.04, -30.4) * mm, "end": v(-18.09, -30.58) * mm});
            skLineSegment(sketch, "E694", {"start": v(-18.09, -30.58) * mm, "end": v(-18.15, -30.77) * mm});
            skLineSegment(sketch, "E695", {"start": v(-18.15, -30.77) * mm, "end": v(-18.24, -30.94) * mm});
            skLineSegment(sketch, "E696", {"start": v(-18.24, -30.94) * mm, "end": v(-18.34, -31.11) * mm});
            skLineSegment(sketch, "E697", {"start": v(-18.34, -31.11) * mm, "end": v(-18.45, -31.27) * mm});
            skLineSegment(sketch, "E698", {"start": v(-18.45, -31.27) * mm, "end": v(-18.59, -31.41) * mm});
            skLineSegment(sketch, "E699", {"start": v(-18.59, -31.41) * mm, "end": v(-18.73, -31.55) * mm});
            skLineSegment(sketch, "E700", {"start": v(-18.73, -31.55) * mm, "end": v(-18.89, -31.66) * mm});
            skLineSegment(sketch, "E701", {"start": v(-18.89, -31.66) * mm, "end": v(-19.06, -31.76) * mm});
            skLineSegment(sketch, "E702", {"start": v(-19.06, -31.76) * mm, "end": v(-19.24, -31.85) * mm});
            skLineSegment(sketch, "E703", {"start": v(-19.24, -31.85) * mm, "end": v(-19.42, -31.91) * mm});
            skLineSegment(sketch, "E704", {"start": v(-19.42, -31.91) * mm, "end": v(-19.61, -31.96) * mm});
            skLineSegment(sketch, "E705", {"start": v(-19.61, -31.96) * mm, "end": v(-19.8, -32) * mm});
            skLineSegment(sketch, "E706", {"start": v(-19.8, -32) * mm, "end": v(-20, -32) * mm});
            skLineSegment(sketch, "E707", {"start": v(-20, -32) * mm, "end": v(-20.2, -32) * mm});
            skLineSegment(sketch, "E708", {"start": v(-40.25, -52.49) * mm, "end": v(-40.49, -52.45) * mm});
            skLineSegment(sketch, "E709", {"start": v(-40.49, -52.45) * mm, "end": v(-40.73, -52.4) * mm});
            skLineSegment(sketch, "E710", {"start": v(-40.73, -52.4) * mm, "end": v(-40.96, -52.3) * mm});
            skLineSegment(sketch, "E711", {"start": v(-40.96, -52.3) * mm, "end": v(-41.18, -52.2) * mm});
            skLineSegment(sketch, "E712", {"start": v(-41.18, -52.2) * mm, "end": v(-41.39, -52.08) * mm});
            skLineSegment(sketch, "E713", {"start": v(-41.39, -52.08) * mm, "end": v(-41.59, -51.93) * mm});
            skLineSegment(sketch, "E714", {"start": v(-41.59, -51.93) * mm, "end": v(-41.77, -51.77) * mm});
            skLineSegment(sketch, "E715", {"start": v(-41.77, -51.77) * mm, "end": v(-41.93, -51.59) * mm});
            skLineSegment(sketch, "E716", {"start": v(-41.93, -51.59) * mm, "end": v(-42.08, -51.39) * mm});
            skLineSegment(sketch, "E717", {"start": v(-42.08, -51.39) * mm, "end": v(-42.2, -51.18) * mm});
            skLineSegment(sketch, "E718", {"start": v(-42.2, -51.18) * mm, "end": v(-42.31, -50.96) * mm});
            skLineSegment(sketch, "E719", {"start": v(-42.31, -50.96) * mm, "end": v(-42.4, -50.73) * mm});
            skLineSegment(sketch, "E720", {"start": v(-42.4, -50.73) * mm, "end": v(-42.45, -50.49) * mm});
            skLineSegment(sketch, "E721", {"start": v(-42.45, -50.49) * mm, "end": v(-42.49, -50.25) * mm});
            skLineSegment(sketch, "E722", {"start": v(-42.49, -50.25) * mm, "end": v(-42.5, -50) * mm});
            skLineSegment(sketch, "E723", {"start": v(-42.5, -50) * mm, "end": v(-42.49, -49.76) * mm});
            skLineSegment(sketch, "E724", {"start": v(-42.49, -49.76) * mm, "end": v(-42.45, -49.51) * mm});
            skLineSegment(sketch, "E725", {"start": v(-42.45, -49.51) * mm, "end": v(-42.4, -49.27) * mm});
            skLineSegment(sketch, "E726", {"start": v(-42.4, -49.27) * mm, "end": v(-42.31, -49.04) * mm});
            skLineSegment(sketch, "E727", {"start": v(-42.31, -49.04) * mm, "end": v(-42.2, -48.82) * mm});
            skLineSegment(sketch, "E728", {"start": v(-42.2, -48.82) * mm, "end": v(-42.08, -48.61) * mm});
            skLineSegment(sketch, "E729", {"start": v(-42.08, -48.61) * mm, "end": v(-41.93, -48.41) * mm});
            skLineSegment(sketch, "E730", {"start": v(-41.93, -48.41) * mm, "end": v(-41.77, -48.23) * mm});
            skLineSegment(sketch, "E731", {"start": v(-41.77, -48.23) * mm, "end": v(-41.59, -48.07) * mm});
            skLineSegment(sketch, "E732", {"start": v(-41.59, -48.07) * mm, "end": v(-41.39, -47.92) * mm});
            skLineSegment(sketch, "E733", {"start": v(-41.39, -47.92) * mm, "end": v(-41.18, -47.8) * mm});
            skLineSegment(sketch, "E734", {"start": v(-41.18, -47.8) * mm, "end": v(-40.96, -47.7) * mm});
            skLineSegment(sketch, "E735", {"start": v(-40.96, -47.7) * mm, "end": v(-40.73, -47.6) * mm});
            skLineSegment(sketch, "E736", {"start": v(-40.73, -47.6) * mm, "end": v(-40.49, -47.55) * mm});
            skLineSegment(sketch, "E737", {"start": v(-40.49, -47.55) * mm, "end": v(-40.25, -47.51) * mm});
            skLineSegment(sketch, "E738", {"start": v(-40.25, -47.51) * mm, "end": v(-40, -47.5) * mm});
            skLineSegment(sketch, "E739", {"start": v(-40, -47.5) * mm, "end": v(-39.75, -47.51) * mm});
            skLineSegment(sketch, "E740", {"start": v(-39.75, -47.51) * mm, "end": v(-39.51, -47.55) * mm});
            skLineSegment(sketch, "E741", {"start": v(-39.51, -47.55) * mm, "end": v(-39.27, -47.6) * mm});
            skLineSegment(sketch, "E742", {"start": v(-39.27, -47.6) * mm, "end": v(-39.04, -47.7) * mm});
            skLineSegment(sketch, "E743", {"start": v(-39.04, -47.7) * mm, "end": v(-38.82, -47.8) * mm});
            skLineSegment(sketch, "E744", {"start": v(-38.82, -47.8) * mm, "end": v(-38.61, -47.92) * mm});
            skLineSegment(sketch, "E745", {"start": v(-38.61, -47.92) * mm, "end": v(-38.41, -48.07) * mm});
            skLineSegment(sketch, "E746", {"start": v(-38.41, -48.07) * mm, "end": v(-38.23, -48.23) * mm});
            skLineSegment(sketch, "E747", {"start": v(-38.23, -48.23) * mm, "end": v(-38.07, -48.41) * mm});
            skLineSegment(sketch, "E748", {"start": v(-38.07, -48.41) * mm, "end": v(-37.92, -48.61) * mm});
            skLineSegment(sketch, "E749", {"start": v(-37.92, -48.61) * mm, "end": v(-37.8, -48.82) * mm});
            skLineSegment(sketch, "E750", {"start": v(-37.8, -48.82) * mm, "end": v(-37.69, -49.04) * mm});
            skLineSegment(sketch, "E751", {"start": v(-37.69, -49.04) * mm, "end": v(-37.6, -49.27) * mm});
            skLineSegment(sketch, "E752", {"start": v(-37.6, -49.27) * mm, "end": v(-37.55, -49.51) * mm});
            skLineSegment(sketch, "E753", {"start": v(-37.55, -49.51) * mm, "end": v(-37.51, -49.76) * mm});
            skLineSegment(sketch, "E754", {"start": v(-37.51, -49.76) * mm, "end": v(-37.5, -50) * mm});
            skLineSegment(sketch, "E755", {"start": v(-37.5, -50) * mm, "end": v(-37.51, -50.25) * mm});
            skLineSegment(sketch, "E756", {"start": v(-37.51, -50.25) * mm, "end": v(-37.55, -50.49) * mm});
            skLineSegment(sketch, "E757", {"start": v(-37.55, -50.49) * mm, "end": v(-37.6, -50.73) * mm});
            skLineSegment(sketch, "E758", {"start": v(-37.6, -50.73) * mm, "end": v(-37.69, -50.96) * mm});
            skLineSegment(sketch, "E759", {"start": v(-37.69, -50.96) * mm, "end": v(-37.8, -51.18) * mm});
            skLineSegment(sketch, "E760", {"start": v(-37.8, -51.18) * mm, "end": v(-37.92, -51.39) * mm});
            skLineSegment(sketch, "E761", {"start": v(-37.92, -51.39) * mm, "end": v(-38.07, -51.59) * mm});
            skLineSegment(sketch, "E762", {"start": v(-38.07, -51.59) * mm, "end": v(-38.23, -51.77) * mm});
            skLineSegment(sketch, "E763", {"start": v(-38.23, -51.77) * mm, "end": v(-38.41, -51.93) * mm});
            skLineSegment(sketch, "E764", {"start": v(-38.41, -51.93) * mm, "end": v(-38.61, -52.08) * mm});
            skLineSegment(sketch, "E765", {"start": v(-38.61, -52.08) * mm, "end": v(-38.82, -52.2) * mm});
            skLineSegment(sketch, "E766", {"start": v(-38.82, -52.2) * mm, "end": v(-39.04, -52.3) * mm});
            skLineSegment(sketch, "E767", {"start": v(-39.04, -52.3) * mm, "end": v(-39.27, -52.4) * mm});
            skLineSegment(sketch, "E768", {"start": v(-39.27, -52.4) * mm, "end": v(-39.51, -52.45) * mm});
            skLineSegment(sketch, "E769", {"start": v(-39.51, -52.45) * mm, "end": v(-39.75, -52.49) * mm});
            skLineSegment(sketch, "E770", {"start": v(-39.75, -52.49) * mm, "end": v(-40, -52.5) * mm});
            skLineSegment(sketch, "E771", {"start": v(-40, -52.5) * mm, "end": v(-40.25, -52.49) * mm});
            skLineSegment(sketch, "E772", {"start": v(33.85, -62.54) * mm, "end": v(33.7, -62.52) * mm});
            skLineSegment(sketch, "E773", {"start": v(33.7, -62.52) * mm, "end": v(33.55, -62.48) * mm});
            skLineSegment(sketch, "E774", {"start": v(33.55, -62.48) * mm, "end": v(33.4, -62.43) * mm});
            skLineSegment(sketch, "E775", {"start": v(33.4, -62.43) * mm, "end": v(33.27, -62.37) * mm});
            skLineSegment(sketch, "E776", {"start": v(33.27, -62.37) * mm, "end": v(33.14, -62.29) * mm});
            skLineSegment(sketch, "E777", {"start": v(33.14, -62.29) * mm, "end": v(33.02, -62.2) * mm});
            skLineSegment(sketch, "E778", {"start": v(33.02, -62.2) * mm, "end": v(32.9, -62.1) * mm});
            skLineSegment(sketch, "E779", {"start": v(32.9, -62.1) * mm, "end": v(32.8, -61.98) * mm});
            skLineSegment(sketch, "E780", {"start": v(32.8, -61.98) * mm, "end": v(32.71, -61.86) * mm});
            skLineSegment(sketch, "E781", {"start": v(32.71, -61.86) * mm, "end": v(32.63, -61.73) * mm});
            skLineSegment(sketch, "E782", {"start": v(32.63, -61.73) * mm, "end": v(32.57, -61.6) * mm});
            skLineSegment(sketch, "E783", {"start": v(32.57, -61.6) * mm, "end": v(32.52, -61.45) * mm});
            skLineSegment(sketch, "E784", {"start": v(32.52, -61.45) * mm, "end": v(32.48, -61.3) * mm});
            skLineSegment(sketch, "E785", {"start": v(32.48, -61.3) * mm, "end": v(32.46, -61.15) * mm});
            skLineSegment(sketch, "E786", {"start": v(32.46, -61.15) * mm, "end": v(32.45, -61) * mm});
            skLineSegment(sketch, "E787", {"start": v(32.45, -61) * mm, "end": v(32.46, -60.85) * mm});
            skLineSegment(sketch, "E788", {"start": v(32.46, -60.85) * mm, "end": v(32.48, -60.7) * mm});
            skLineSegment(sketch, "E789", {"start": v(32.48, -60.7) * mm, "end": v(32.52, -60.55) * mm});
            skLineSegment(sketch, "E790", {"start": v(32.52, -60.55) * mm, "end": v(32.57, -60.4) * mm});
            skLineSegment(sketch, "E791", {"start": v(32.57, -60.4) * mm, "end": v(32.63, -60.27) * mm});
            skLineSegment(sketch, "E792", {"start": v(32.63, -60.27) * mm, "end": v(32.71, -60.14) * mm});
            skLineSegment(sketch, "E793", {"start": v(32.71, -60.14) * mm, "end": v(32.8, -60.02) * mm});
            skLineSegment(sketch, "E794", {"start": v(32.8, -60.02) * mm, "end": v(32.9, -59.9) * mm});
            skLineSegment(sketch, "E795", {"start": v(32.9, -59.9) * mm, "end": v(33.02, -59.8) * mm});
            skLineSegment(sketch, "E796", {"start": v(33.02, -59.8) * mm, "end": v(33.14, -59.71) * mm});
            skLineSegment(sketch, "E797", {"start": v(33.14, -59.71) * mm, "end": v(33.27, -59.63) * mm});
            skLineSegment(sketch, "E798", {"start": v(33.27, -59.63) * mm, "end": v(33.4, -59.57) * mm});
            skLineSegment(sketch, "E799", {"start": v(33.4, -59.57) * mm, "end": v(33.55, -59.52) * mm});
            skLineSegment(sketch, "E800", {"start": v(33.55, -59.52) * mm, "end": v(33.7, -59.48) * mm});
            skLineSegment(sketch, "E801", {"start": v(33.7, -59.48) * mm, "end": v(33.85, -59.46) * mm});
            skLineSegment(sketch, "E802", {"start": v(33.85, -59.46) * mm, "end": v(34, -59.45) * mm});
            skLineSegment(sketch, "E803", {"start": v(34, -59.45) * mm, "end": v(34.15, -59.46) * mm});
            skLineSegment(sketch, "E804", {"start": v(34.15, -59.46) * mm, "end": v(34.3, -59.48) * mm});
            skLineSegment(sketch, "E805", {"start": v(34.3, -59.48) * mm, "end": v(34.45, -59.52) * mm});
            skLineSegment(sketch, "E806", {"start": v(34.45, -59.52) * mm, "end": v(34.6, -59.57) * mm});
            skLineSegment(sketch, "E807", {"start": v(34.6, -59.57) * mm, "end": v(34.73, -59.63) * mm});
            skLineSegment(sketch, "E808", {"start": v(34.73, -59.63) * mm, "end": v(34.86, -59.71) * mm});
            skLineSegment(sketch, "E809", {"start": v(34.86, -59.71) * mm, "end": v(34.98, -59.8) * mm});
            skLineSegment(sketch, "E810", {"start": v(34.98, -59.8) * mm, "end": v(35.1, -59.9) * mm});
            skLineSegment(sketch, "E811", {"start": v(35.1, -59.9) * mm, "end": v(35.2, -60.02) * mm});
            skLineSegment(sketch, "E812", {"start": v(35.2, -60.02) * mm, "end": v(35.29, -60.14) * mm});
            skLineSegment(sketch, "E813", {"start": v(35.29, -60.14) * mm, "end": v(35.37, -60.27) * mm});
            skLineSegment(sketch, "E814", {"start": v(35.37, -60.27) * mm, "end": v(35.43, -60.4) * mm});
            skLineSegment(sketch, "E815", {"start": v(35.43, -60.4) * mm, "end": v(35.48, -60.55) * mm});
            skLineSegment(sketch, "E816", {"start": v(35.48, -60.55) * mm, "end": v(35.52, -60.7) * mm});
            skLineSegment(sketch, "E817", {"start": v(35.52, -60.7) * mm, "end": v(35.54, -60.85) * mm});
            skLineSegment(sketch, "E818", {"start": v(35.54, -60.85) * mm, "end": v(35.55, -61) * mm});
            skLineSegment(sketch, "E819", {"start": v(35.55, -61) * mm, "end": v(35.54, -61.15) * mm});
            skLineSegment(sketch, "E820", {"start": v(35.54, -61.15) * mm, "end": v(35.52, -61.3) * mm});
            skLineSegment(sketch, "E821", {"start": v(35.52, -61.3) * mm, "end": v(35.48, -61.45) * mm});
            skLineSegment(sketch, "E822", {"start": v(35.48, -61.45) * mm, "end": v(35.43, -61.6) * mm});
            skLineSegment(sketch, "E823", {"start": v(35.43, -61.6) * mm, "end": v(35.37, -61.73) * mm});
            skLineSegment(sketch, "E824", {"start": v(35.37, -61.73) * mm, "end": v(35.29, -61.86) * mm});
            skLineSegment(sketch, "E825", {"start": v(35.29, -61.86) * mm, "end": v(35.2, -61.98) * mm});
            skLineSegment(sketch, "E826", {"start": v(35.2, -61.98) * mm, "end": v(35.1, -62.1) * mm});
            skLineSegment(sketch, "E827", {"start": v(35.1, -62.1) * mm, "end": v(34.98, -62.2) * mm});
            skLineSegment(sketch, "E828", {"start": v(34.98, -62.2) * mm, "end": v(34.86, -62.29) * mm});
            skLineSegment(sketch, "E829", {"start": v(34.86, -62.29) * mm, "end": v(34.73, -62.37) * mm});
            skLineSegment(sketch, "E830", {"start": v(34.73, -62.37) * mm, "end": v(34.6, -62.43) * mm});
            skLineSegment(sketch, "E831", {"start": v(34.6, -62.43) * mm, "end": v(34.45, -62.48) * mm});
            skLineSegment(sketch, "E832", {"start": v(34.45, -62.48) * mm, "end": v(34.3, -62.52) * mm});
            skLineSegment(sketch, "E833", {"start": v(34.3, -62.52) * mm, "end": v(34.15, -62.54) * mm});
            skLineSegment(sketch, "E834", {"start": v(34.15, -62.54) * mm, "end": v(34, -62.55) * mm});
            skLineSegment(sketch, "E835", {"start": v(34, -62.55) * mm, "end": v(33.85, -62.54) * mm});
            skLineSegment(sketch, "E836", {"start": v(97.85, -88.54) * mm, "end": v(97.7, -88.52) * mm});
            skLineSegment(sketch, "E837", {"start": v(97.7, -88.52) * mm, "end": v(97.55, -88.48) * mm});
            skLineSegment(sketch, "E838", {"start": v(97.55, -88.48) * mm, "end": v(97.4, -88.43) * mm});
            skLineSegment(sketch, "E839", {"start": v(97.4, -88.43) * mm, "end": v(97.27, -88.37) * mm});
            skLineSegment(sketch, "E840", {"start": v(97.27, -88.37) * mm, "end": v(97.14, -88.29) * mm});
            skLineSegment(sketch, "E841", {"start": v(97.14, -88.29) * mm, "end": v(97.02, -88.2) * mm});
            skLineSegment(sketch, "E842", {"start": v(97.02, -88.2) * mm, "end": v(96.9, -88.1) * mm});
            skLineSegment(sketch, "E843", {"start": v(96.9, -88.1) * mm, "end": v(96.8, -87.98) * mm});
            skLineSegment(sketch, "E844", {"start": v(96.8, -87.98) * mm, "end": v(96.71, -87.86) * mm});
            skLineSegment(sketch, "E845", {"start": v(96.71, -87.86) * mm, "end": v(96.63, -87.73) * mm});
            skLineSegment(sketch, "E846", {"start": v(96.63, -87.73) * mm, "end": v(96.57, -87.6) * mm});
            skLineSegment(sketch, "E847", {"start": v(96.57, -87.6) * mm, "end": v(96.52, -87.45) * mm});
            skLineSegment(sketch, "E848", {"start": v(96.52, -87.45) * mm, "end": v(96.48, -87.3) * mm});
            skLineSegment(sketch, "E849", {"start": v(96.48, -87.3) * mm, "end": v(96.46, -87.15) * mm});
            skLineSegment(sketch, "E850", {"start": v(96.46, -87.15) * mm, "end": v(96.45, -87) * mm});
            skLineSegment(sketch, "E851", {"start": v(96.45, -87) * mm, "end": v(96.46, -86.85) * mm});
            skLineSegment(sketch, "E852", {"start": v(96.46, -86.85) * mm, "end": v(96.48, -86.7) * mm});
            skLineSegment(sketch, "E853", {"start": v(96.48, -86.7) * mm, "end": v(96.52, -86.55) * mm});
            skLineSegment(sketch, "E854", {"start": v(96.52, -86.55) * mm, "end": v(96.57, -86.4) * mm});
            skLineSegment(sketch, "E855", {"start": v(96.57, -86.4) * mm, "end": v(96.63, -86.27) * mm});
            skLineSegment(sketch, "E856", {"start": v(96.63, -86.27) * mm, "end": v(96.71, -86.14) * mm});
            skLineSegment(sketch, "E857", {"start": v(96.71, -86.14) * mm, "end": v(96.8, -86.02) * mm});
            skLineSegment(sketch, "E858", {"start": v(96.8, -86.02) * mm, "end": v(96.9, -85.9) * mm});
            skLineSegment(sketch, "E859", {"start": v(96.9, -85.9) * mm, "end": v(97.02, -85.8) * mm});
            skLineSegment(sketch, "E860", {"start": v(97.02, -85.8) * mm, "end": v(97.14, -85.71) * mm});
            skLineSegment(sketch, "E861", {"start": v(97.14, -85.71) * mm, "end": v(97.27, -85.63) * mm});
            skLineSegment(sketch, "E862", {"start": v(97.27, -85.63) * mm, "end": v(97.4, -85.57) * mm});
            skLineSegment(sketch, "E863", {"start": v(97.4, -85.57) * mm, "end": v(97.55, -85.52) * mm});
            skLineSegment(sketch, "E864", {"start": v(97.55, -85.52) * mm, "end": v(97.7, -85.48) * mm});
            skLineSegment(sketch, "E865", {"start": v(97.7, -85.48) * mm, "end": v(97.85, -85.46) * mm});
            skLineSegment(sketch, "E866", {"start": v(97.85, -85.46) * mm, "end": v(98, -85.45) * mm});
            skLineSegment(sketch, "E867", {"start": v(98, -85.45) * mm, "end": v(98.15, -85.46) * mm});
            skLineSegment(sketch, "E868", {"start": v(98.15, -85.46) * mm, "end": v(98.3, -85.48) * mm});
            skLineSegment(sketch, "E869", {"start": v(98.3, -85.48) * mm, "end": v(98.45, -85.52) * mm});
            skLineSegment(sketch, "E870", {"start": v(98.45, -85.52) * mm, "end": v(98.6, -85.57) * mm});
            skLineSegment(sketch, "E871", {"start": v(98.6, -85.57) * mm, "end": v(98.73, -85.63) * mm});
            skLineSegment(sketch, "E872", {"start": v(98.73, -85.63) * mm, "end": v(98.86, -85.71) * mm});
            skLineSegment(sketch, "E873", {"start": v(98.86, -85.71) * mm, "end": v(98.98, -85.8) * mm});
            skLineSegment(sketch, "E874", {"start": v(98.98, -85.8) * mm, "end": v(99.1, -85.9) * mm});
            skLineSegment(sketch, "E875", {"start": v(99.1, -85.9) * mm, "end": v(99.2, -86.02) * mm});
            skLineSegment(sketch, "E876", {"start": v(99.2, -86.02) * mm, "end": v(99.29, -86.14) * mm});
            skLineSegment(sketch, "E877", {"start": v(99.29, -86.14) * mm, "end": v(99.37, -86.27) * mm});
            skLineSegment(sketch, "E878", {"start": v(99.37, -86.27) * mm, "end": v(99.43, -86.4) * mm});
            skLineSegment(sketch, "E879", {"start": v(99.43, -86.4) * mm, "end": v(99.48, -86.55) * mm});
            skLineSegment(sketch, "E880", {"start": v(99.48, -86.55) * mm, "end": v(99.52, -86.7) * mm});
            skLineSegment(sketch, "E881", {"start": v(99.52, -86.7) * mm, "end": v(99.54, -86.85) * mm});
            skLineSegment(sketch, "E882", {"start": v(99.54, -86.85) * mm, "end": v(99.55, -87) * mm});
            skLineSegment(sketch, "E883", {"start": v(99.55, -87) * mm, "end": v(99.54, -87.15) * mm});
            skLineSegment(sketch, "E884", {"start": v(99.54, -87.15) * mm, "end": v(99.52, -87.3) * mm});
            skLineSegment(sketch, "E885", {"start": v(99.52, -87.3) * mm, "end": v(99.48, -87.45) * mm});
            skLineSegment(sketch, "E886", {"start": v(99.48, -87.45) * mm, "end": v(99.43, -87.6) * mm});
            skLineSegment(sketch, "E887", {"start": v(99.43, -87.6) * mm, "end": v(99.37, -87.73) * mm});
            skLineSegment(sketch, "E888", {"start": v(99.37, -87.73) * mm, "end": v(99.29, -87.86) * mm});
            skLineSegment(sketch, "E889", {"start": v(99.29, -87.86) * mm, "end": v(99.2, -87.98) * mm});
            skLineSegment(sketch, "E890", {"start": v(99.2, -87.98) * mm, "end": v(99.1, -88.1) * mm});
            skLineSegment(sketch, "E891", {"start": v(99.1, -88.1) * mm, "end": v(98.98, -88.2) * mm});
            skLineSegment(sketch, "E892", {"start": v(98.98, -88.2) * mm, "end": v(98.86, -88.29) * mm});
            skLineSegment(sketch, "E893", {"start": v(98.86, -88.29) * mm, "end": v(98.73, -88.37) * mm});
            skLineSegment(sketch, "E894", {"start": v(98.73, -88.37) * mm, "end": v(98.6, -88.43) * mm});
            skLineSegment(sketch, "E895", {"start": v(98.6, -88.43) * mm, "end": v(98.45, -88.48) * mm});
            skLineSegment(sketch, "E896", {"start": v(98.45, -88.48) * mm, "end": v(98.3, -88.52) * mm});
            skLineSegment(sketch, "E897", {"start": v(98.3, -88.52) * mm, "end": v(98.15, -88.54) * mm});
            skLineSegment(sketch, "E898", {"start": v(98.15, -88.54) * mm, "end": v(98, -88.55) * mm});
            skLineSegment(sketch, "E899", {"start": v(98, -88.55) * mm, "end": v(97.85, -88.54) * mm});
            skSolve(sketch);
        }
        {
            var Q0;
            Q0=makeQuery(id+"F0.imprint","IMPRINT",FACE,{"disambiguationData":[TD([[makeQuery(id+"F0.imprint","IMPRINT",EDGE,{"derivedFrom":sQuery(id+"F0.wireOp",EDGE,"E0")}),1.0]])]});
            extrude(context, id + "F1", {"entities" : qUnion([Q0]), "depth" : 6 * mm, "offsetDistance" : 25 * mm});
        }
    });
